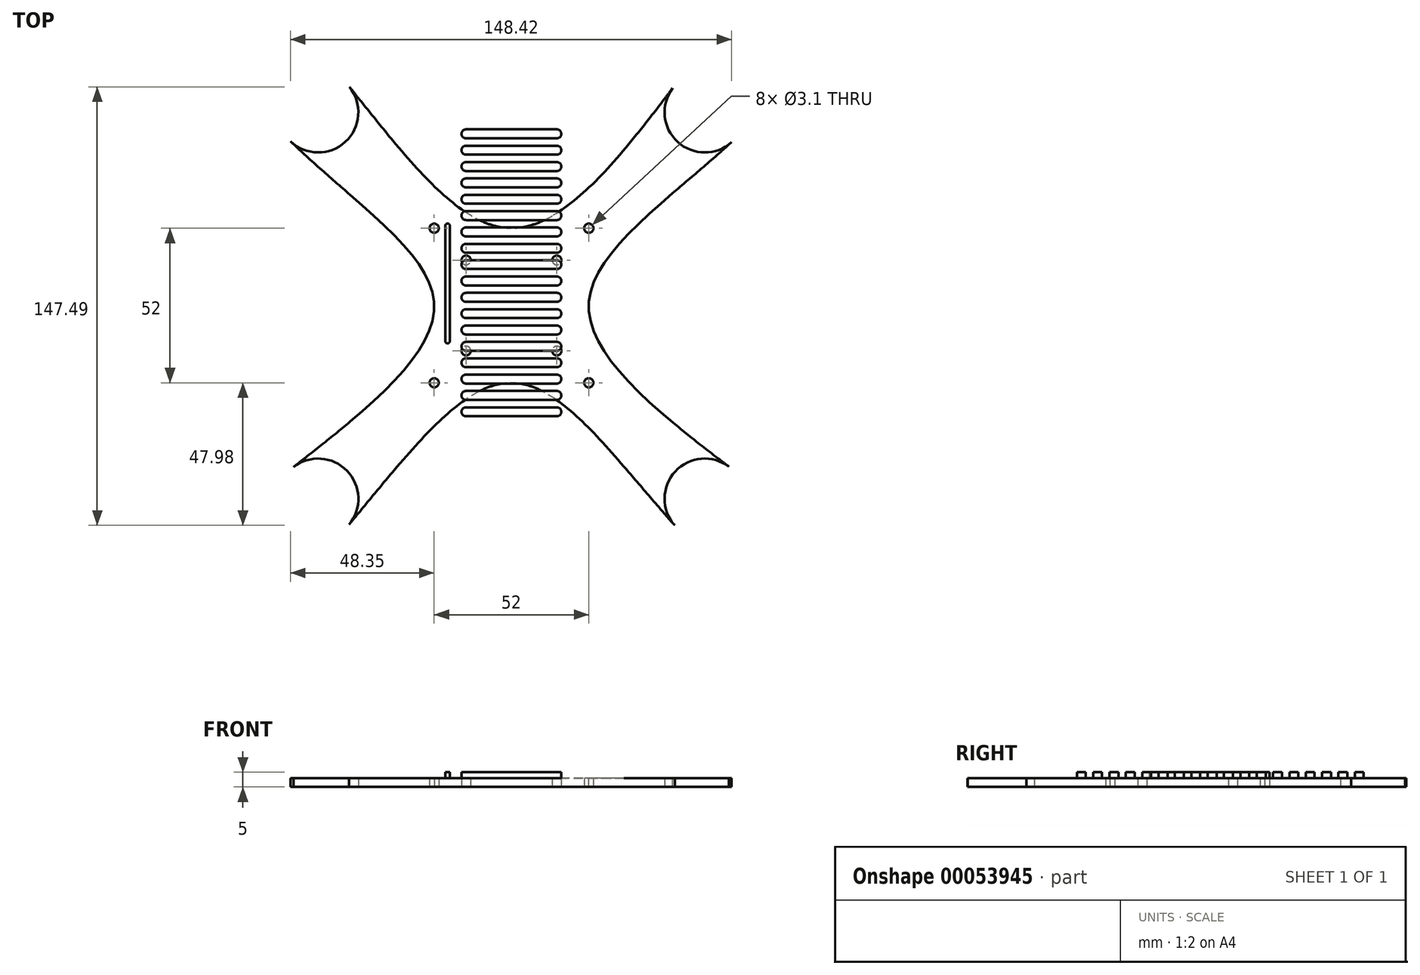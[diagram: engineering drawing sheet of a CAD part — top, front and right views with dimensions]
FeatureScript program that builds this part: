
annotation { "Feature Type Name" : "Feature", "Feature Type Description" : "" }
export const myFeature = defineFeature(function(context is Context, id is Id, definition is map)
    precondition{}
    {
        {
            var Q0;
            Q0=qCreatedBy(makeId("Top.planeOp"),FACE);
            var sketch = newSketch(context, id + "F0", { "sketchPlane" : qUnion([Q0])});
            skLineSegment(sketch, "E0.rect.bottom", {"start": v(-65, -65) * mm, "end": v(65, -65) * mm, "construction": true});
            skLineSegment(sketch, "E0.rect.top", {"start": v(-65, 65) * mm, "end": v(65, 65) * mm, "construction": true});
            skLineSegment(sketch, "E0.rect.left", {"start": v(-65, -65) * mm, "end": v(-65, 65) * mm, "construction": true});
            skLineSegment(sketch, "E0.rect.right", {"start": v(65, -65) * mm, "end": v(65, 65) * mm, "construction": true});
            skPoint(sketch, "E0.rect.middle", {"position": v(0, 0) * mm});
            skCircle(sketch, "E1", {"center": v(-65, 65) * mm, "radius": 50.75 * mm, "construction": true});
            skCircle(sketch, "E2", {"center": v(65, 65) * mm, "radius": 50.75 * mm, "construction": true});
            skCircle(sketch, "E3", {"center": v(65, -65) * mm, "radius": 50.75 * mm, "construction": true});
            skCircle(sketch, "E4", {"center": v(-65, -65) * mm, "radius": 50.75 * mm, "construction": true});
            skArc(sketch, "E5", {"start": v(-77.6, 69.86) * mm, "mid": v(-55.45, 55.45) * mm, "end": v(-69.86, 77.6) * mm});
            skArc(sketch, "E6", {"start": v(69.86, 77.6) * mm, "mid": v(55.45, 55.45) * mm, "end": v(77.6, 69.86) * mm});
            skArc(sketch, "E7", {"start": v(77.6, -69.86) * mm, "mid": v(55.45, -55.45) * mm, "end": v(69.86, -77.6) * mm});
            skArc(sketch, "E8", {"start": v(-69.86, -77.6) * mm, "mid": v(-55.45, -55.45) * mm, "end": v(-77.6, -69.86) * mm});
            skLineSegment(sketch, "E9.rect.bottom", {"start": v(26, -26) * mm, "end": v(-26, -26) * mm, "construction": true});
            skLineSegment(sketch, "E9.rect.top", {"start": v(26, 26) * mm, "end": v(-26, 26) * mm, "construction": true});
            skLineSegment(sketch, "E9.rect.left", {"start": v(26, -26) * mm, "end": v(26, 26) * mm, "construction": true});
            skLineSegment(sketch, "E9.rect.right", {"start": v(-26, -26) * mm, "end": v(-26, 26) * mm, "construction": true});
            skFitSpline(sketch, "E10", {"points": [v(-74.35, 55.26) * mm, v(-26, 0) * mm, v(-73.36, -54.4) * mm], "startDerivative": vector(138.42, -132.82) * mm, "endDerivative": vector(-144.38, -113.88) * mm});
            skFitSpline(sketch, "E11", {"points": [v(74.07, 55) * mm, v(26, 0) * mm, v(73.19, -54.27) * mm], "startDerivative": vector(-139.4, -126.45) * mm, "endDerivative": vector(143.94, -109.76) * mm});
            skFitSpline(sketch, "E12", {"points": [v(54.92, -73.98) * mm, v(0, -26) * mm, v(-54.66, -73.68) * mm], "startDerivative": vector(-126.12, 141.5) * mm, "endDerivative": vector(-120.97, -144.22) * mm});
            skFitSpline(sketch, "E13", {"points": [v(-54.52, 73.5) * mm, v(0, 26) * mm, v(54.26, 73.17) * mm], "startDerivative": vector(114.67, -141.24) * mm, "endDerivative": vector(108.47, 142.58) * mm});
            skLineSegment(sketch, "E14.rect.bottom", {"start": v(-15.25, -15.25) * mm, "end": v(15.25, -15.25) * mm, "construction": true});
            skLineSegment(sketch, "E14.rect.top", {"start": v(-15.25, 15.25) * mm, "end": v(15.25, 15.25) * mm, "construction": true});
            skLineSegment(sketch, "E14.rect.left", {"start": v(-15.25, -15.25) * mm, "end": v(-15.25, 15.25) * mm, "construction": true});
            skLineSegment(sketch, "E14.rect.right", {"start": v(15.25, -15.25) * mm, "end": v(15.25, 15.25) * mm, "construction": true});
            skArc(sketch, "E15", {"start": v(-4.8, 73.17) * mm, "mid": v(-17.28, 102.6) * mm, "end": v(-42.96, 121.6) * mm});
            skArc(sketch, "E16", {"start": v(4.8, 73.17) * mm, "mid": v(17.28, 102.6) * mm, "end": v(42.96, 121.6) * mm});
            skArc(sketch, "E17", {"start": v(73.17, -4.8) * mm, "mid": v(102.6, -17.28) * mm, "end": v(121.6, -42.96) * mm});
            skArc(sketch, "E18", {"start": v(-4.8, -73.17) * mm, "mid": v(-17.28, -102.6) * mm, "end": v(-42.96, -121.6) * mm});
            skArc(sketch, "E19.0", {"start": v(-4.6, 90.96) * mm, "mid": v(-19.8, 112.75) * mm, "end": v(-42.39, 126.74) * mm});
            skArc(sketch, "E20.0", {"start": v(4.6, 90.96) * mm, "mid": v(19.8, 112.75) * mm, "end": v(42.39, 126.74) * mm});
            skLineSegment(sketch, "E21.0.left", {"start": v(-47.27, 67.5) * mm, "end": v(-9.76, 67.5) * mm});
            skLineSegment(sketch, "E22.1.right", {"start": v(-47.17, -67.5) * mm, "end": v(-9.76, -67.5) * mm});
            skLineSegment(sketch, "E23.0.right", {"start": v(67.5, -47.45) * mm, "end": v(67.5, -9.76) * mm});
            skArc(sketch, "E24.trimOffspring", {"start": v(-4.6, -90.96) * mm, "mid": v(-19.8, -112.75) * mm, "end": v(-42.39, -126.74) * mm});
            skArc(sketch, "E25.trimOffspring", {"start": v(90.96, -4.6) * mm, "mid": v(112.75, -19.8) * mm, "end": v(126.74, -42.39) * mm});
            skLineSegment(sketch, "E26.trimOffspring", {"start": v(-35.06, 62.5) * mm, "end": v(35.61, 62.5) * mm});
            skLineSegment(sketch, "E27.trimOffspring", {"start": v(-62.5, -35.22) * mm, "end": v(-62.5, 33.4) * mm});
            skLineSegment(sketch, "E28.trimOffspring", {"start": v(-67.5, -47.35) * mm, "end": v(-67.5, -9.76) * mm});
            skLineSegment(sketch, "E29.trimOffspring", {"start": v(-34.67, -62.5) * mm, "end": v(34.1, -62.5) * mm});
            skLineSegment(sketch, "E30.trimOffspring", {"start": v(62.5, -35.55) * mm, "end": v(62.5, 34) * mm});
            skPoint(sketch, "E31.visualSharp", {"position": v(-74.9, 0) * mm});
            skArc(sketch, "E31.filletArc", {"start": v(-90.96, -4.6) * mm, "mid": v(-87.94, 0) * mm, "end": v(-90.96, 4.6) * mm});
            skPoint(sketch, "E32.visualSharp", {"position": v(0, 74.9) * mm});
            skArc(sketch, "E32.filletArc", {"start": v(-4.6, 90.96) * mm, "mid": v(0, 87.94) * mm, "end": v(4.6, 90.96) * mm});
            skPoint(sketch, "E33.visualSharp", {"position": v(74.9, 0) * mm});
            skArc(sketch, "E33.filletArc", {"start": v(90.96, 4.6) * mm, "mid": v(87.94, 0) * mm, "end": v(90.96, -4.6) * mm});
            skPoint(sketch, "E34.visualSharp", {"position": v(0, -74.9) * mm});
            skArc(sketch, "E34.filletArc", {"start": v(4.6, -90.96) * mm, "mid": v(0, -87.94) * mm, "end": v(-4.6, -90.96) * mm});
            skLineSegment(sketch, "E35.trimOffspring", {"start": v(9.76, 67.5) * mm, "end": v(47.45, 67.5) * mm});
            skLineSegment(sketch, "E36.trimOffspring", {"start": v(67.5, 9.76) * mm, "end": v(67.5, 46.9) * mm});
            skLineSegment(sketch, "E37.trimOffspring", {"start": v(-67.5, 9.76) * mm, "end": v(-67.5, 46.68) * mm});
            skLineSegment(sketch, "E38.trimOffspring", {"start": v(9.76, -67.5) * mm, "end": v(46.96, -67.5) * mm});
            skPoint(sketch, "E39.visualSharp", {"position": v(67.5, 4.3) * mm});
            skArc(sketch, "E39.filletArc", {"start": v(67.5, 9.76) * mm, "mid": v(69.21, 6) * mm, "end": v(73.17, 4.8) * mm});
            skPoint(sketch, "E40.visualSharp", {"position": v(67.5, -4.3) * mm});
            skArc(sketch, "E40.filletArc", {"start": v(73.17, -4.8) * mm, "mid": v(69.21, -6) * mm, "end": v(67.5, -9.76) * mm});
            skPoint(sketch, "E41.visualSharp", {"position": v(4.3, 67.5) * mm});
            skArc(sketch, "E41.filletArc", {"start": v(4.8, 73.17) * mm, "mid": v(6, 69.21) * mm, "end": v(9.76, 67.5) * mm});
            skPoint(sketch, "E42.visualSharp", {"position": v(-4.3, 67.5) * mm});
            skArc(sketch, "E42.filletArc", {"start": v(-9.76, 67.5) * mm, "mid": v(-6, 69.21) * mm, "end": v(-4.8, 73.17) * mm});
            skPoint(sketch, "E43.visualSharp", {"position": v(-67.5, 4.3) * mm});
            skArc(sketch, "E43.filletArc", {"start": v(-73.17, 4.8) * mm, "mid": v(-69.21, 6) * mm, "end": v(-67.5, 9.76) * mm});
            skPoint(sketch, "E44.visualSharp", {"position": v(-67.5, -4.3) * mm});
            skArc(sketch, "E44.filletArc", {"start": v(-67.5, -9.76) * mm, "mid": v(-69.21, -6) * mm, "end": v(-73.17, -4.8) * mm});
            skPoint(sketch, "E45.visualSharp", {"position": v(-4.3, -67.5) * mm});
            skArc(sketch, "E45.filletArc", {"start": v(-4.8, -73.17) * mm, "mid": v(-6, -69.21) * mm, "end": v(-9.76, -67.5) * mm});
            skPoint(sketch, "E46.visualSharp", {"position": v(4.3, -67.5) * mm});
            skArc(sketch, "E46.filletArc", {"start": v(9.76, -67.5) * mm, "mid": v(6, -69.21) * mm, "end": v(4.8, -73.17) * mm});
            skPoint(sketch, "E47.visualSharp", {"position": v(46.05, 62.5) * mm});
            skArc(sketch, "E47.filletArc", {"start": v(39.46, 54.3) * mm, "mid": v(40.14, 59.63) * mm, "end": v(35.61, 62.5) * mm});
            skPoint(sketch, "E48.visualSharp", {"position": v(-45.64, 62.5) * mm});
            skArc(sketch, "E48.filletArc", {"start": v(-35.06, 62.5) * mm, "mid": v(-39.6, 59.61) * mm, "end": v(-38.89, 54.28) * mm});
            skPoint(sketch, "E49.visualSharp", {"position": v(-62.5, 44.43) * mm});
            skArc(sketch, "E49.filletArc", {"start": v(-54.2, 37.17) * mm, "mid": v(-59.57, 37.96) * mm, "end": v(-62.5, 33.4) * mm});
            skPoint(sketch, "E50.visualSharp", {"position": v(-62.5, -45.8) * mm});
            skArc(sketch, "E50.filletArc", {"start": v(-62.5, -35.22) * mm, "mid": v(-59.6, -39.76) * mm, "end": v(-54.28, -39.05) * mm});
            skPoint(sketch, "E51.visualSharp", {"position": v(-45.38, -62.5) * mm});
            skArc(sketch, "E51.filletArc", {"start": v(-38.48, -54.26) * mm, "mid": v(-39.21, -59.6) * mm, "end": v(-34.67, -62.5) * mm});
            skPoint(sketch, "E52.visualSharp", {"position": v(44.96, -62.5) * mm});
            skArc(sketch, "E52.filletArc", {"start": v(34.1, -62.5) * mm, "mid": v(38.64, -59.58) * mm, "end": v(37.88, -54.23) * mm});
            skPoint(sketch, "E53.visualSharp", {"position": v(62.5, -46.02) * mm});
            skArc(sketch, "E53.filletArc", {"start": v(54.3, -39.4) * mm, "mid": v(59.62, -40.08) * mm, "end": v(62.5, -35.55) * mm});
            skPoint(sketch, "E54.visualSharp", {"position": v(62.5, 44.86) * mm});
            skArc(sketch, "E54.filletArc", {"start": v(62.5, 34) * mm, "mid": v(59.58, 38.54) * mm, "end": v(54.24, 37.78) * mm});
            skPoint(sketch, "E55.visualSharp", {"position": v(67.5, 49.17) * mm});
            skArc(sketch, "E55.filletArc", {"start": v(69.2, 50.66) * mm, "mid": v(67.95, 48.96) * mm, "end": v(67.5, 46.9) * mm});
            skPoint(sketch, "E56.visualSharp", {"position": v(49.92, 67.5) * mm});
            skArc(sketch, "E56.filletArc", {"start": v(47.45, 67.5) * mm, "mid": v(49.67, 68.02) * mm, "end": v(51.43, 69.46) * mm});
            skPoint(sketch, "E57.visualSharp", {"position": v(-49.67, 67.5) * mm});
            skArc(sketch, "E57.filletArc", {"start": v(-51.17, 69.36) * mm, "mid": v(-49.43, 67.99) * mm, "end": v(-47.27, 67.5) * mm});
            skPoint(sketch, "E58.visualSharp", {"position": v(-67.5, 48.9) * mm});
            skArc(sketch, "E58.filletArc", {"start": v(-67.5, 46.68) * mm, "mid": v(-67.92, 48.7) * mm, "end": v(-69.12, 50.37) * mm});
            skPoint(sketch, "E59.visualSharp", {"position": v(-67.5, -49.77) * mm});
            skArc(sketch, "E59.filletArc", {"start": v(-69.4, -51.28) * mm, "mid": v(-68, -49.53) * mm, "end": v(-67.5, -47.35) * mm});
            skPoint(sketch, "E60.visualSharp", {"position": v(-49.52, -67.5) * mm});
            skArc(sketch, "E60.filletArc", {"start": v(-47.17, -67.5) * mm, "mid": v(-49.3, -67.97) * mm, "end": v(-51.02, -69.3) * mm});
            skPoint(sketch, "E61.visualSharp", {"position": v(49.25, -67.5) * mm});
            skArc(sketch, "E61.filletArc", {"start": v(50.74, -69.22) * mm, "mid": v(49.04, -67.95) * mm, "end": v(46.96, -67.5) * mm});
            skPoint(sketch, "E62.visualSharp", {"position": v(67.5, -49.9) * mm});
            skArc(sketch, "E62.filletArc", {"start": v(67.5, -47.45) * mm, "mid": v(68.02, -49.66) * mm, "end": v(69.46, -51.41) * mm});
            skLineSegment(sketch, "E63", {"start": v(-65, 65) * mm, "end": v(-111.5, 111.5) * mm, "construction": true});
            skLineSegment(sketch, "E64", {"start": v(65, 65) * mm, "end": v(111.5, 111.5) * mm, "construction": true});
            skLineSegment(sketch, "E65", {"start": v(65, -65) * mm, "end": v(111.5, -111.5) * mm, "construction": true});
            skLineSegment(sketch, "E66", {"start": v(-65, -65) * mm, "end": v(-111.5, -111.5) * mm, "construction": true});
            skLineSegment(sketch, "E67.0.left", {"start": v(-78.73, 75.2) * mm, "end": v(-105.83, 102.3) * mm});
            skLineSegment(sketch, "E67.0.right", {"start": v(-75.2, 78.73) * mm, "end": v(-102.3, 105.83) * mm});
            skLineSegment(sketch, "E67.1.left", {"start": v(75.2, 78.73) * mm, "end": v(102.3, 105.83) * mm});
            skLineSegment(sketch, "E67.1.right", {"start": v(78.73, 75.2) * mm, "end": v(105.83, 102.3) * mm});
            skLineSegment(sketch, "E67.2.left", {"start": v(78.73, -75.2) * mm, "end": v(105.83, -102.3) * mm});
            skLineSegment(sketch, "E67.2.right", {"start": v(75.2, -78.73) * mm, "end": v(102.3, -105.83) * mm});
            skLineSegment(sketch, "E67.3.left", {"start": v(-75.2, -78.73) * mm, "end": v(-102.3, -105.83) * mm});
            skLineSegment(sketch, "E67.3.right", {"start": v(-78.73, -75.2) * mm, "end": v(-105.83, -102.3) * mm});
            skLineSegment(sketch, "E68.trimOffspring", {"start": v(-113.23, 109.7) * mm, "end": v(-113.26, 109.72) * mm});
            skLineSegment(sketch, "E69.trimOffspring", {"start": v(-109.7, 113.23) * mm, "end": v(-109.72, 113.26) * mm});
            skArc(sketch, "E70.trimOffspring", {"start": v(-113.35, 101.79) * mm, "mid": v(-123.85, 80.08) * mm, "end": v(-125.08, 56) * mm});
            skLineSegment(sketch, "E71.trimOffspring", {"start": v(113.23, 109.7) * mm, "end": v(113.26, 109.72) * mm});
            skLineSegment(sketch, "E72.trimOffspring", {"start": v(109.7, 113.23) * mm, "end": v(109.72, 113.26) * mm});
            skArc(sketch, "E73.trimOffspring", {"start": v(113.35, 101.79) * mm, "mid": v(123.85, 80.08) * mm, "end": v(125.08, 56) * mm});
            skLineSegment(sketch, "E74.trimOffspring", {"start": v(113.23, -109.7) * mm, "end": v(113.26, -109.72) * mm});
            skLineSegment(sketch, "E75.trimOffspring", {"start": v(109.7, -113.23) * mm, "end": v(109.72, -113.26) * mm});
            skArc(sketch, "E76.trimOffspring", {"start": v(101.79, -113.35) * mm, "mid": v(80.08, -123.85) * mm, "end": v(56, -125.08) * mm});
            skArc(sketch, "E77.trimOffspring", {"start": v(-113.35, -101.79) * mm, "mid": v(-123.85, -80.08) * mm, "end": v(-125.08, -56) * mm});
            skLineSegment(sketch, "E78.trimOffspring", {"start": v(-113.23, -109.7) * mm, "end": v(-113.26, -109.72) * mm});
            skLineSegment(sketch, "E79.trimOffspring", {"start": v(-109.7, -113.23) * mm, "end": v(-109.72, -113.26) * mm});
            skPoint(sketch, "E80.visualSharp", {"position": v(106.15, 109.69) * mm});
            skArc(sketch, "E80.filletArc", {"start": v(102.3, 105.83) * mm, "mid": v(103.75, 109.7) * mm, "end": v(101.79, 113.35) * mm});
            skPoint(sketch, "E81.visualSharp", {"position": v(109.69, 106.15) * mm});
            skArc(sketch, "E81.filletArc", {"start": v(113.35, 101.79) * mm, "mid": v(109.7, 103.75) * mm, "end": v(105.83, 102.3) * mm});
            skPoint(sketch, "E82.visualSharp", {"position": v(76.15, 72.61) * mm});
            skArc(sketch, "E82.filletArc", {"start": v(78.73, 75.2) * mm, "mid": v(77.37, 72.7) * mm, "end": v(77.6, 69.86) * mm});
            skPoint(sketch, "E83.visualSharp", {"position": v(72.61, 76.15) * mm});
            skArc(sketch, "E83.filletArc", {"start": v(69.86, 77.6) * mm, "mid": v(72.7, 77.37) * mm, "end": v(75.2, 78.73) * mm});
            skPoint(sketch, "E84.visualSharp", {"position": v(-72.61, 76.15) * mm});
            skArc(sketch, "E84.filletArc", {"start": v(-75.2, 78.73) * mm, "mid": v(-72.7, 77.37) * mm, "end": v(-69.86, 77.6) * mm});
            skPoint(sketch, "E85.visualSharp", {"position": v(-76.15, 72.61) * mm});
            skArc(sketch, "E85.filletArc", {"start": v(-77.6, 69.86) * mm, "mid": v(-77.37, 72.7) * mm, "end": v(-78.73, 75.2) * mm});
            skPoint(sketch, "E86.visualSharp", {"position": v(-106.15, 109.69) * mm});
            skArc(sketch, "E86.filletArc", {"start": v(-101.79, 113.35) * mm, "mid": v(-103.75, 109.7) * mm, "end": v(-102.3, 105.83) * mm});
            skPoint(sketch, "E87.visualSharp", {"position": v(-109.69, 106.15) * mm});
            skArc(sketch, "E87.filletArc", {"start": v(-105.83, 102.3) * mm, "mid": v(-109.7, 103.75) * mm, "end": v(-113.35, 101.79) * mm});
            skPoint(sketch, "E88.visualSharp", {"position": v(76.15, -72.61) * mm});
            skArc(sketch, "E88.filletArc", {"start": v(77.6, -69.86) * mm, "mid": v(77.37, -72.7) * mm, "end": v(78.73, -75.2) * mm});
            skPoint(sketch, "E89.visualSharp", {"position": v(109.69, -106.15) * mm});
            skArc(sketch, "E89.filletArc", {"start": v(105.83, -102.3) * mm, "mid": v(109.7, -103.75) * mm, "end": v(113.35, -101.79) * mm});
            skPoint(sketch, "E90.visualSharp", {"position": v(106.15, -109.69) * mm});
            skArc(sketch, "E90.filletArc", {"start": v(101.79, -113.35) * mm, "mid": v(103.75, -109.7) * mm, "end": v(102.3, -105.83) * mm});
            skPoint(sketch, "E91.visualSharp", {"position": v(72.61, -76.15) * mm});
            skArc(sketch, "E91.filletArc", {"start": v(75.2, -78.73) * mm, "mid": v(72.7, -77.37) * mm, "end": v(69.86, -77.6) * mm});
            skPoint(sketch, "E92.visualSharp", {"position": v(-72.61, -76.15) * mm});
            skArc(sketch, "E92.filletArc", {"start": v(-69.86, -77.6) * mm, "mid": v(-72.7, -77.37) * mm, "end": v(-75.2, -78.73) * mm});
            skPoint(sketch, "E93.visualSharp", {"position": v(-76.15, -72.61) * mm});
            skArc(sketch, "E93.filletArc", {"start": v(-78.73, -75.2) * mm, "mid": v(-77.37, -72.7) * mm, "end": v(-77.6, -69.86) * mm});
            skPoint(sketch, "E94.visualSharp", {"position": v(-106.15, -109.69) * mm});
            skArc(sketch, "E94.filletArc", {"start": v(-102.3, -105.83) * mm, "mid": v(-103.75, -109.7) * mm, "end": v(-101.79, -113.35) * mm});
            skPoint(sketch, "E95.visualSharp", {"position": v(-109.69, -106.15) * mm});
            skArc(sketch, "E95.filletArc", {"start": v(-113.35, -101.79) * mm, "mid": v(-109.7, -103.75) * mm, "end": v(-105.83, -102.3) * mm});
            skCircle(sketch, "E96", {"center": v(-15.25, 15.25) * mm, "radius": 1.55 * mm});
            skCircle(sketch, "E97", {"center": v(15.25, 15.25) * mm, "radius": 1.55 * mm});
            skCircle(sketch, "E98", {"center": v(15.25, -15.25) * mm, "radius": 1.55 * mm});
            skCircle(sketch, "E99", {"center": v(-15.25, -15.25) * mm, "radius": 1.55 * mm});
            skCircle(sketch, "E100", {"center": v(-65, 65) * mm, "radius": 4.5 * mm});
            skCircle(sketch, "E101", {"center": v(65, 65) * mm, "radius": 4.5 * mm});
            skCircle(sketch, "E102", {"center": v(65, -65) * mm, "radius": 4.5 * mm});
            skCircle(sketch, "E103", {"center": v(-65, -65) * mm, "radius": 4.5 * mm});
            skCircle(sketch, "E104", {"center": v(-26, 26) * mm, "radius": 1.55 * mm});
            skCircle(sketch, "E105", {"center": v(26, 26) * mm, "radius": 1.55 * mm});
            skCircle(sketch, "E106", {"center": v(-26, -26) * mm, "radius": 1.55 * mm});
            skCircle(sketch, "E107", {"center": v(26, -26) * mm, "radius": 1.55 * mm});
            skLineSegment(sketch, "E108", {"start": v(65, 57) * mm, "end": v(65, 55.5) * mm});
            skLineSegment(sketch, "E109", {"start": v(57, 65) * mm, "end": v(55.5, 65) * mm});
            skLineSegment(sketch, "E110", {"start": v(73, 65) * mm, "end": v(74.5, 65) * mm});
            skLineSegment(sketch, "E111", {"start": v(65, 73) * mm, "end": v(65, 74.5) * mm});
            skArc(sketch, "E112.0.startCap", {"start": v(73, 63.5) * mm, "mid": v(71.5, 65) * mm, "end": v(73, 66.5) * mm});
            skArc(sketch, "E112.0.endCap", {"start": v(74.5, 66.5) * mm, "mid": v(76, 65) * mm, "end": v(74.5, 63.5) * mm});
            skLineSegment(sketch, "E112.0.left", {"start": v(73, 66.5) * mm, "end": v(74.5, 66.5) * mm});
            skLineSegment(sketch, "E112.0.right", {"start": v(73, 63.5) * mm, "end": v(74.5, 63.5) * mm});
            skArc(sketch, "E113.0.startCap", {"start": v(66.5, 73) * mm, "mid": v(65, 71.5) * mm, "end": v(63.5, 73) * mm});
            skArc(sketch, "E113.0.endCap", {"start": v(63.5, 74.5) * mm, "mid": v(65, 76) * mm, "end": v(66.5, 74.5) * mm});
            skLineSegment(sketch, "E113.0.left", {"start": v(63.5, 73) * mm, "end": v(63.5, 74.5) * mm});
            skLineSegment(sketch, "E113.0.right", {"start": v(66.5, 73) * mm, "end": v(66.5, 74.5) * mm});
            skArc(sketch, "E114.0.startCap", {"start": v(57, 66.5) * mm, "mid": v(58.5, 65) * mm, "end": v(57, 63.5) * mm});
            skArc(sketch, "E114.0.endCap", {"start": v(55.5, 63.5) * mm, "mid": v(54, 65) * mm, "end": v(55.5, 66.5) * mm});
            skLineSegment(sketch, "E114.0.left", {"start": v(57, 63.5) * mm, "end": v(55.5, 63.5) * mm});
            skLineSegment(sketch, "E114.0.right", {"start": v(57, 66.5) * mm, "end": v(55.5, 66.5) * mm});
            skArc(sketch, "E115.0.startCap", {"start": v(63.5, 57) * mm, "mid": v(65, 58.5) * mm, "end": v(66.5, 57) * mm});
            skArc(sketch, "E115.0.endCap", {"start": v(66.5, 55.5) * mm, "mid": v(65, 54) * mm, "end": v(63.5, 55.5) * mm});
            skLineSegment(sketch, "E115.0.left", {"start": v(66.5, 57) * mm, "end": v(66.5, 55.5) * mm});
            skLineSegment(sketch, "E115.0.right", {"start": v(63.5, 57) * mm, "end": v(63.5, 55.5) * mm});
            skLineSegment(sketch, "E116", {"start": v(0, 153.86) * mm, "end": v(0, -113.26) * mm, "construction": true});
            skArc(sketch, "E117.MirrorCS", {"start": v(-66.5, 55.5) * mm, "mid": v(-65, 54) * mm, "end": v(-63.5, 55.5) * mm});
            skLineSegment(sketch, "E118.MirrorCS", {"start": v(-66.5, 57) * mm, "end": v(-66.5, 55.5) * mm});
            skLineSegment(sketch, "E119.MirrorCS", {"start": v(-63.5, 57) * mm, "end": v(-63.5, 55.5) * mm});
            skArc(sketch, "E120.MirrorCS", {"start": v(-63.5, 57) * mm, "mid": v(-65, 58.5) * mm, "end": v(-66.5, 57) * mm});
            skLineSegment(sketch, "E121.MirrorCS", {"start": v(-65, 57) * mm, "end": v(-65, 55.5) * mm});
            skArc(sketch, "E122.MirrorCS", {"start": v(-73, 63.5) * mm, "mid": v(-71.5, 65) * mm, "end": v(-73, 66.5) * mm});
            skLineSegment(sketch, "E123.MirrorCS", {"start": v(-73, 63.5) * mm, "end": v(-74.5, 63.5) * mm});
            skLineSegment(sketch, "E124.MirrorCS", {"start": v(-73, 66.5) * mm, "end": v(-74.5, 66.5) * mm});
            skLineSegment(sketch, "E125.MirrorCS", {"start": v(-73, 65) * mm, "end": v(-74.5, 65) * mm});
            skArc(sketch, "E126.MirrorCS", {"start": v(-74.5, 66.5) * mm, "mid": v(-76, 65) * mm, "end": v(-74.5, 63.5) * mm});
            skLineSegment(sketch, "E127.MirrorCS", {"start": v(-57, 63.5) * mm, "end": v(-55.5, 63.5) * mm});
            skArc(sketch, "E128.MirrorCS", {"start": v(-55.5, 63.5) * mm, "mid": v(-54, 65) * mm, "end": v(-55.5, 66.5) * mm});
            skLineSegment(sketch, "E129.MirrorCS", {"start": v(-66.5, 73) * mm, "end": v(-66.5, 74.5) * mm});
            skLineSegment(sketch, "E130.MirrorCS", {"start": v(-57, 66.5) * mm, "end": v(-55.5, 66.5) * mm});
            skArc(sketch, "E131.MirrorCS", {"start": v(-57, 66.5) * mm, "mid": v(-58.5, 65) * mm, "end": v(-57, 63.5) * mm});
            skArc(sketch, "E132.MirrorCS", {"start": v(-63.5, 74.5) * mm, "mid": v(-65, 76) * mm, "end": v(-66.5, 74.5) * mm});
            skArc(sketch, "E133.MirrorCS", {"start": v(-66.5, 73) * mm, "mid": v(-65, 71.5) * mm, "end": v(-63.5, 73) * mm});
            skLineSegment(sketch, "E134", {"start": v(-63.5, 74.5) * mm, "end": v(-63.5, 73) * mm});
            skLineSegment(sketch, "E135", {"start": v(125.68, 0) * mm, "end": v(-117.28, 0) * mm, "construction": true});
            skArc(sketch, "E136.MirrorCS", {"start": v(-66.5, -55.5) * mm, "mid": v(-65, -54) * mm, "end": v(-63.5, -55.5) * mm});
            skLineSegment(sketch, "E137.MirrorCS", {"start": v(-63.5, -57) * mm, "end": v(-63.5, -55.5) * mm});
            skLineSegment(sketch, "E138.MirrorCS", {"start": v(-66.5, -57) * mm, "end": v(-66.5, -55.5) * mm});
            skLineSegment(sketch, "E139.MirrorCS", {"start": v(-65, -57) * mm, "end": v(-65, -55.5) * mm});
            skArc(sketch, "E140.MirrorCS", {"start": v(-63.5, -57) * mm, "mid": v(-65, -58.5) * mm, "end": v(-66.5, -57) * mm});
            skArc(sketch, "E141.MirrorCS", {"start": v(-74.5, -66.5) * mm, "mid": v(-76, -65) * mm, "end": v(-74.5, -63.5) * mm});
            skLineSegment(sketch, "E142.MirrorCS", {"start": v(-73, -65) * mm, "end": v(-74.5, -65) * mm});
            skLineSegment(sketch, "E143.MirrorCS", {"start": v(-73, -66.5) * mm, "end": v(-74.5, -66.5) * mm});
            skLineSegment(sketch, "E144.MirrorCS", {"start": v(-73, -63.5) * mm, "end": v(-74.5, -63.5) * mm});
            skArc(sketch, "E145.MirrorCS", {"start": v(-73, -63.5) * mm, "mid": v(-71.5, -65) * mm, "end": v(-73, -66.5) * mm});
            skLineSegment(sketch, "E146.MirrorCS", {"start": v(-57, -63.5) * mm, "end": v(-55.5, -63.5) * mm});
            skLineSegment(sketch, "E147.MirrorCS", {"start": v(-57, -66.5) * mm, "end": v(-55.5, -66.5) * mm});
            skArc(sketch, "E148.MirrorCS", {"start": v(-57, -66.5) * mm, "mid": v(-58.5, -65) * mm, "end": v(-57, -63.5) * mm});
            skArc(sketch, "E149.MirrorCS", {"start": v(-55.5, -63.5) * mm, "mid": v(-54, -65) * mm, "end": v(-55.5, -66.5) * mm});
            skArc(sketch, "E150.MirrorCS", {"start": v(-66.5, -73) * mm, "mid": v(-65, -71.5) * mm, "end": v(-63.5, -73) * mm});
            skArc(sketch, "E151.MirrorCS", {"start": v(-63.5, -74.5) * mm, "mid": v(-65, -76) * mm, "end": v(-66.5, -74.5) * mm});
            skLineSegment(sketch, "E152.MirrorCS", {"start": v(-66.5, -73) * mm, "end": v(-66.5, -74.5) * mm});
            skLineSegment(sketch, "E153.MirrorCS", {"start": v(-63.5, -74.5) * mm, "end": v(-63.5, -73) * mm});
            skLineSegment(sketch, "E154.MirrorCS", {"start": v(65, -57) * mm, "end": v(65, -55.5) * mm});
            skLineSegment(sketch, "E155.MirrorCS", {"start": v(63.5, -57) * mm, "end": v(63.5, -55.5) * mm});
            skLineSegment(sketch, "E156.MirrorCS", {"start": v(66.5, -57) * mm, "end": v(66.5, -55.5) * mm});
            skArc(sketch, "E157.MirrorCS", {"start": v(66.5, -55.5) * mm, "mid": v(65, -54) * mm, "end": v(63.5, -55.5) * mm});
            skArc(sketch, "E158.MirrorCS", {"start": v(63.5, -57) * mm, "mid": v(65, -58.5) * mm, "end": v(66.5, -57) * mm});
            skArc(sketch, "E159.MirrorCS", {"start": v(74.5, -66.5) * mm, "mid": v(76, -65) * mm, "end": v(74.5, -63.5) * mm});
            skLineSegment(sketch, "E160.MirrorCS", {"start": v(73, -65) * mm, "end": v(74.5, -65) * mm});
            skLineSegment(sketch, "E161.MirrorCS", {"start": v(73, -63.5) * mm, "end": v(74.5, -63.5) * mm});
            skArc(sketch, "E162.MirrorCS", {"start": v(73, -63.5) * mm, "mid": v(71.5, -65) * mm, "end": v(73, -66.5) * mm});
            skLineSegment(sketch, "E163.MirrorCS", {"start": v(73, -66.5) * mm, "end": v(74.5, -66.5) * mm});
            skLineSegment(sketch, "E164.MirrorCS", {"start": v(57, -66.5) * mm, "end": v(55.5, -66.5) * mm});
            skLineSegment(sketch, "E165.MirrorCS", {"start": v(57, -63.5) * mm, "end": v(55.5, -63.5) * mm});
            skArc(sketch, "E166.MirrorCS", {"start": v(55.5, -63.5) * mm, "mid": v(54, -65) * mm, "end": v(55.5, -66.5) * mm});
            skLineSegment(sketch, "E167.MirrorCS", {"start": v(57, -65) * mm, "end": v(55.5, -65) * mm});
            skArc(sketch, "E168.MirrorCS", {"start": v(57, -66.5) * mm, "mid": v(58.5, -65) * mm, "end": v(57, -63.5) * mm});
            skArc(sketch, "E169.MirrorCS", {"start": v(63.5, -74.5) * mm, "mid": v(65, -76) * mm, "end": v(66.5, -74.5) * mm});
            skLineSegment(sketch, "E170.MirrorCS", {"start": v(65, -73) * mm, "end": v(65, -74.5) * mm});
            skLineSegment(sketch, "E171.MirrorCS", {"start": v(63.5, -73) * mm, "end": v(63.5, -74.5) * mm});
            skLineSegment(sketch, "E172.MirrorCS", {"start": v(66.5, -73) * mm, "end": v(66.5, -74.5) * mm});
            skArc(sketch, "E173.MirrorCS", {"start": v(66.5, -73) * mm, "mid": v(65, -71.5) * mm, "end": v(63.5, -73) * mm});
            skArc(sketch, "E174", {"start": v(-122.17, 48.12) * mm, "mid": v(-122.26, 49.77) * mm, "end": v(-123, 51.24) * mm});
            skArc(sketch, "E175.MirrorC", {"start": v(-46.45, 122.85) * mm, "mid": v(-49.77, 122.26) * mm, "end": v(-52.36, 124.42) * mm});
            skArc(sketch, "E176.MirrorC", {"start": v(-130, 49.75) * mm, "mid": v(-129.99, 47.71) * mm, "end": v(-128.98, 45.94) * mm});
            skArc(sketch, "E177.MirrorC", {"start": v(-48.12, 122.17) * mm, "mid": v(-49.77, 122.26) * mm, "end": v(-51.24, 123) * mm});
            skArc(sketch, "E178.MirrorC", {"start": v(130, 49.75) * mm, "mid": v(129.99, 47.71) * mm, "end": v(128.98, 45.94) * mm});
            skArc(sketch, "E179.MirrorC", {"start": v(48.12, 122.17) * mm, "mid": v(49.77, 122.26) * mm, "end": v(51.24, 123) * mm});
            skArc(sketch, "E180.MirrorC", {"start": v(122.17, -48.12) * mm, "mid": v(122.26, -49.77) * mm, "end": v(123, -51.24) * mm});
            skArc(sketch, "E181.MirrorC", {"start": v(49.75, -130) * mm, "mid": v(47.71, -129.99) * mm, "end": v(45.94, -128.98) * mm});
            skArc(sketch, "E182.MirrorC", {"start": v(-48.12, -122.17) * mm, "mid": v(-49.77, -122.26) * mm, "end": v(-51.24, -123) * mm});
            skArc(sketch, "E183.MirrorC", {"start": v(-122.17, -48.12) * mm, "mid": v(-122.26, -49.77) * mm, "end": v(-123, -51.24) * mm});
            skArc(sketch, "E184.trimOffspring", {"start": v(-126.74, 42.39) * mm, "mid": v(-112.75, 19.8) * mm, "end": v(-90.96, 4.6) * mm});
            skArc(sketch, "E185.trimOffspring", {"start": v(-121.6, 42.96) * mm, "mid": v(-102.6, 17.28) * mm, "end": v(-73.17, 4.8) * mm});
            skArc(sketch, "E186.trimOffspring", {"start": v(-122.85, 46.45) * mm, "mid": v(-122.26, 49.77) * mm, "end": v(-124.42, 52.36) * mm});
            skArc(sketch, "E187.trimOffspring", {"start": v(-129.28, 51.2) * mm, "mid": v(-129.99, 47.71) * mm, "end": v(-127.65, 45.04) * mm});
            skArc(sketch, "E188.trimOffspring", {"start": v(-53.95, 129.81) * mm, "mid": v(-111.5, 111.5) * mm, "end": v(-129.81, 53.95) * mm});
            skArc(sketch, "E189.trimOffspring", {"start": v(-56, 125.08) * mm, "mid": v(-80.08, 123.85) * mm, "end": v(-101.79, 113.35) * mm});
            skArc(sketch, "E190.trimOffspring", {"start": v(-51.2, 129.28) * mm, "mid": v(-47.71, 129.99) * mm, "end": v(-45.04, 127.65) * mm});
            skArc(sketch, "E191.trimOffspring", {"start": v(-49.75, 130) * mm, "mid": v(-47.71, 129.99) * mm, "end": v(-45.94, 128.98) * mm});
            skArc(sketch, "E192.trimOffspring", {"start": v(49.75, 130) * mm, "mid": v(47.71, 129.99) * mm, "end": v(45.94, 128.98) * mm});
            skArc(sketch, "E193.trimOffspring", {"start": v(53.95, 129.81) * mm, "mid": v(111.5, 111.5) * mm, "end": v(129.81, 53.95) * mm});
            skArc(sketch, "E194.trimOffspring", {"start": v(56, 125.08) * mm, "mid": v(80.08, 123.85) * mm, "end": v(101.79, 113.35) * mm});
            skArc(sketch, "E195.trimOffspring", {"start": v(121.6, 42.96) * mm, "mid": v(102.6, 17.28) * mm, "end": v(73.17, 4.8) * mm});
            skArc(sketch, "E196.trimOffspring", {"start": v(126.74, 42.39) * mm, "mid": v(112.75, 19.8) * mm, "end": v(90.96, 4.6) * mm});
            skArc(sketch, "E197.trimOffspring", {"start": v(122.17, 48.12) * mm, "mid": v(122.26, 49.77) * mm, "end": v(123, 51.24) * mm});
            skArc(sketch, "E198.trimOffspring", {"start": v(-130, -49.75) * mm, "mid": v(-129.99, -47.71) * mm, "end": v(-128.98, -45.94) * mm});
            skArc(sketch, "E199.trimOffspring", {"start": v(-126.74, -42.39) * mm, "mid": v(-112.75, -19.8) * mm, "end": v(-90.96, -4.6) * mm});
            skArc(sketch, "E200.trimOffspring", {"start": v(-121.6, -42.96) * mm, "mid": v(-102.6, -17.28) * mm, "end": v(-73.17, -4.8) * mm});
            skArc(sketch, "E201.trimOffspring", {"start": v(-56, -125.08) * mm, "mid": v(-80.08, -123.85) * mm, "end": v(-101.79, -113.35) * mm});
            skArc(sketch, "E202.trimOffspring", {"start": v(-53.95, -129.81) * mm, "mid": v(-111.5, -111.5) * mm, "end": v(-129.81, -53.95) * mm});
            skArc(sketch, "E203.trimOffspring", {"start": v(-49.75, -130) * mm, "mid": v(-47.71, -129.99) * mm, "end": v(-45.94, -128.98) * mm});
            skArc(sketch, "E204.trimOffspring", {"start": v(42.39, -126.74) * mm, "mid": v(19.8, -112.75) * mm, "end": v(4.6, -90.96) * mm});
            skArc(sketch, "E205.trimOffspring", {"start": v(42.96, -121.6) * mm, "mid": v(17.28, -102.6) * mm, "end": v(4.8, -73.17) * mm});
            skArc(sketch, "E206.trimOffspring", {"start": v(48.12, -122.17) * mm, "mid": v(49.77, -122.26) * mm, "end": v(51.24, -123) * mm});
            skArc(sketch, "E207.trimOffspring", {"start": v(130, -49.75) * mm, "mid": v(129.99, -47.71) * mm, "end": v(128.98, -45.94) * mm});
            skArc(sketch, "E208.trimOffspring", {"start": v(129.81, -53.95) * mm, "mid": v(111.5, -111.5) * mm, "end": v(53.95, -129.81) * mm});
            skPoint(sketch, "E209.visualSharp", {"position": v(-45.04, 127.65) * mm});
            skArc(sketch, "E209.filletArc", {"start": v(-45.94, 128.98) * mm, "mid": v(-44.28, 127.67) * mm, "end": v(-42.39, 126.74) * mm});
            skPoint(sketch, "E210.visualSharp", {"position": v(-46.45, 122.85) * mm});
            skArc(sketch, "E210.filletArc", {"start": v(-42.96, 121.6) * mm, "mid": v(-45.5, 122.23) * mm, "end": v(-48.12, 122.17) * mm});
            skPoint(sketch, "E211.visualSharp", {"position": v(-51.2, 129.28) * mm});
            skArc(sketch, "E211.filletArc", {"start": v(-53.95, 129.81) * mm, "mid": v(-51.84, 129.68) * mm, "end": v(-49.75, 130) * mm});
            skPoint(sketch, "E212.visualSharp", {"position": v(-52.36, 124.42) * mm});
            skArc(sketch, "E212.filletArc", {"start": v(-51.24, 123) * mm, "mid": v(-53.48, 124.36) * mm, "end": v(-56, 125.08) * mm});
            skPoint(sketch, "E213.visualSharp", {"position": v(-124.42, 52.36) * mm});
            skArc(sketch, "E213.filletArc", {"start": v(-125.08, 56) * mm, "mid": v(-124.36, 53.48) * mm, "end": v(-123, 51.24) * mm});
            skPoint(sketch, "E214.visualSharp", {"position": v(-122.85, 46.45) * mm});
            skArc(sketch, "E214.filletArc", {"start": v(-122.17, 48.12) * mm, "mid": v(-122.23, 45.5) * mm, "end": v(-121.6, 42.96) * mm});
            skPoint(sketch, "E215.visualSharp", {"position": v(-129.28, 51.2) * mm});
            skArc(sketch, "E215.filletArc", {"start": v(-130, 49.75) * mm, "mid": v(-129.68, 51.84) * mm, "end": v(-129.81, 53.95) * mm});
            skPoint(sketch, "E216.visualSharp", {"position": v(-127.65, 45.04) * mm});
            skArc(sketch, "E216.filletArc", {"start": v(-126.74, 42.39) * mm, "mid": v(-127.67, 44.28) * mm, "end": v(-128.98, 45.94) * mm});
            skPoint(sketch, "E217.visualSharp", {"position": v(45.04, 127.65) * mm});
            skArc(sketch, "E217.filletArc", {"start": v(42.39, 126.74) * mm, "mid": v(44.28, 127.67) * mm, "end": v(45.94, 128.98) * mm});
            skPoint(sketch, "E218.visualSharp", {"position": v(51.2, 129.28) * mm});
            skArc(sketch, "E218.filletArc", {"start": v(49.75, 130) * mm, "mid": v(51.84, 129.68) * mm, "end": v(53.95, 129.81) * mm});
            skPoint(sketch, "E219.visualSharp", {"position": v(52.36, 124.42) * mm});
            skArc(sketch, "E219.filletArc", {"start": v(56, 125.08) * mm, "mid": v(53.48, 124.36) * mm, "end": v(51.24, 123) * mm});
            skPoint(sketch, "E220.visualSharp", {"position": v(46.45, 122.85) * mm});
            skArc(sketch, "E220.filletArc", {"start": v(48.12, 122.17) * mm, "mid": v(45.5, 122.23) * mm, "end": v(42.96, 121.6) * mm});
            skPoint(sketch, "E221.visualSharp", {"position": v(124.42, 52.36) * mm});
            skArc(sketch, "E221.filletArc", {"start": v(123, 51.24) * mm, "mid": v(124.36, 53.48) * mm, "end": v(125.08, 56) * mm});
            skPoint(sketch, "E222.visualSharp", {"position": v(122.85, 46.45) * mm});
            skArc(sketch, "E222.filletArc", {"start": v(121.6, 42.96) * mm, "mid": v(122.23, 45.5) * mm, "end": v(122.17, 48.12) * mm});
            skPoint(sketch, "E223.visualSharp", {"position": v(127.65, 45.04) * mm});
            skArc(sketch, "E223.filletArc", {"start": v(128.98, 45.94) * mm, "mid": v(127.67, 44.28) * mm, "end": v(126.74, 42.39) * mm});
            skPoint(sketch, "E224.visualSharp", {"position": v(129.28, 51.2) * mm});
            skArc(sketch, "E224.filletArc", {"start": v(129.81, 53.95) * mm, "mid": v(129.68, 51.84) * mm, "end": v(130, 49.75) * mm});
            skArc(sketch, "E225.trimOffspring", {"start": v(125.08, -56) * mm, "mid": v(123.85, -80.08) * mm, "end": v(113.35, -101.79) * mm});
            skPoint(sketch, "E226.visualSharp", {"position": v(127.65, -45.04) * mm});
            skArc(sketch, "E226.filletArc", {"start": v(126.74, -42.39) * mm, "mid": v(127.67, -44.28) * mm, "end": v(128.98, -45.94) * mm});
            skPoint(sketch, "E227.visualSharp", {"position": v(129.28, -51.2) * mm});
            skArc(sketch, "E227.filletArc", {"start": v(130, -49.75) * mm, "mid": v(129.68, -51.84) * mm, "end": v(129.81, -53.95) * mm});
            skPoint(sketch, "E228.visualSharp", {"position": v(124.42, -52.36) * mm});
            skArc(sketch, "E228.filletArc", {"start": v(125.08, -56) * mm, "mid": v(124.36, -53.48) * mm, "end": v(123, -51.24) * mm});
            skPoint(sketch, "E229.visualSharp", {"position": v(122.85, -46.45) * mm});
            skArc(sketch, "E229.filletArc", {"start": v(122.17, -48.12) * mm, "mid": v(122.23, -45.5) * mm, "end": v(121.6, -42.96) * mm});
            skPoint(sketch, "E230.visualSharp", {"position": v(52.36, -124.42) * mm});
            skArc(sketch, "E230.filletArc", {"start": v(51.24, -123) * mm, "mid": v(53.48, -124.36) * mm, "end": v(56, -125.08) * mm});
            skPoint(sketch, "E231.visualSharp", {"position": v(51.2, -129.28) * mm});
            skArc(sketch, "E231.filletArc", {"start": v(53.95, -129.81) * mm, "mid": v(51.84, -129.68) * mm, "end": v(49.75, -130) * mm});
            skPoint(sketch, "E232.visualSharp", {"position": v(45.04, -127.65) * mm});
            skArc(sketch, "E232.filletArc", {"start": v(45.94, -128.98) * mm, "mid": v(44.28, -127.67) * mm, "end": v(42.39, -126.74) * mm});
            skPoint(sketch, "E233.visualSharp", {"position": v(46.45, -122.85) * mm});
            skArc(sketch, "E233.filletArc", {"start": v(42.96, -121.6) * mm, "mid": v(45.5, -122.23) * mm, "end": v(48.12, -122.17) * mm});
            skPoint(sketch, "E234.visualSharp", {"position": v(-46.45, -122.85) * mm});
            skArc(sketch, "E234.filletArc", {"start": v(-48.12, -122.17) * mm, "mid": v(-45.5, -122.23) * mm, "end": v(-42.96, -121.6) * mm});
            skPoint(sketch, "E235.visualSharp", {"position": v(-45.04, -127.65) * mm});
            skArc(sketch, "E235.filletArc", {"start": v(-42.39, -126.74) * mm, "mid": v(-44.28, -127.67) * mm, "end": v(-45.94, -128.98) * mm});
            skPoint(sketch, "E236.visualSharp", {"position": v(-51.2, -129.28) * mm});
            skArc(sketch, "E236.filletArc", {"start": v(-49.75, -130) * mm, "mid": v(-51.84, -129.68) * mm, "end": v(-53.95, -129.81) * mm});
            skPoint(sketch, "E237.visualSharp", {"position": v(-52.36, -124.42) * mm});
            skArc(sketch, "E237.filletArc", {"start": v(-56, -125.08) * mm, "mid": v(-53.48, -124.36) * mm, "end": v(-51.24, -123) * mm});
            skPoint(sketch, "E238.visualSharp", {"position": v(-124.42, -52.36) * mm});
            skArc(sketch, "E238.filletArc", {"start": v(-123, -51.24) * mm, "mid": v(-124.36, -53.48) * mm, "end": v(-125.08, -56) * mm});
            skPoint(sketch, "E239.visualSharp", {"position": v(-122.85, -46.45) * mm});
            skArc(sketch, "E239.filletArc", {"start": v(-121.6, -42.96) * mm, "mid": v(-122.23, -45.5) * mm, "end": v(-122.17, -48.12) * mm});
            skPoint(sketch, "E240.visualSharp", {"position": v(-129.28, -51.2) * mm});
            skArc(sketch, "E240.filletArc", {"start": v(-129.81, -53.95) * mm, "mid": v(-129.68, -51.84) * mm, "end": v(-130, -49.75) * mm});
            skPoint(sketch, "E241.visualSharp", {"position": v(-127.65, -45.04) * mm});
            skArc(sketch, "E241.filletArc", {"start": v(-128.98, -45.94) * mm, "mid": v(-127.67, -44.28) * mm, "end": v(-126.74, -42.39) * mm});
            skCircle(sketch, "E242", {"center": v(-65, 65) * mm, "radius": 63.25 * mm, "construction": true});
            skCircle(sketch, "E243", {"center": v(65, 65) * mm, "radius": 63.25 * mm, "construction": true});
            skCircle(sketch, "E244", {"center": v(-65, -65) * mm, "radius": 63.25 * mm, "construction": true});
            skPoint(sketch, "E245.second.point", {"position": v(-109.7, 103.75) * mm});
            skPoint(sketch, "E245.third.point", {"position": v(-103.7, 108.66) * mm});
            skPoint(sketch, "E246.second.point", {"position": v(103.75, 109.7) * mm});
            skPoint(sketch, "E246.third.point", {"position": v(109.03, 103.75) * mm});
            skPoint(sketch, "E246.third.point.positionSnap0", {"position": v(109.7, 103.75) * mm});
            skPoint(sketch, "E247.second.point", {"position": v(109.7, -103.75) * mm});
            skPoint(sketch, "E247.third.point", {"position": v(103.76, -109.16) * mm});
            skPoint(sketch, "E248.second.point", {"position": v(-109.7, -103.75) * mm});
            skPoint(sketch, "E248.third.point", {"position": v(-103.75, -109.03) * mm});
            skPoint(sketch, "E248.third.point.positionSnap0", {"position": v(-103.75, -109.7) * mm});
            skCircle(sketch, "E249", {"center": v(-108.3, 108.15) * mm, "radius": 1.55 * mm});
            skCircle(sketch, "E250", {"center": v(-48.74, 126.12) * mm, "radius": 1.55 * mm});
            skCircle(sketch, "E251", {"center": v(-126.12, 48.74) * mm, "radius": 1.55 * mm});
            skCircle(sketch, "E252", {"center": v(-126.12, -48.74) * mm, "radius": 1.55 * mm});
            skCircle(sketch, "E253", {"center": v(-108.3, -108.15) * mm, "radius": 1.55 * mm});
            skCircle(sketch, "E254", {"center": v(-48.74, -126.12) * mm, "radius": 1.55 * mm});
            skCircle(sketch, "E255", {"center": v(48.74, -126.12) * mm, "radius": 1.55 * mm});
            skCircle(sketch, "E256", {"center": v(108.28, -108.16) * mm, "radius": 1.55 * mm});
            skCircle(sketch, "E257", {"center": v(126.12, -48.74) * mm, "radius": 1.55 * mm});
            skCircle(sketch, "E258", {"center": v(126.12, 48.74) * mm, "radius": 1.55 * mm});
            skCircle(sketch, "E259", {"center": v(108.15, 108.3) * mm, "radius": 1.55 * mm});
            skCircle(sketch, "E260", {"center": v(48.74, 126.12) * mm, "radius": 1.55 * mm});
            skCircle(sketch, "E261", {"center": v(0, 79.89) * mm, "radius": 1.55 * mm});
            skCircle(sketch, "E262", {"center": v(-79.89, 0) * mm, "radius": 1.55 * mm});
            skCircle(sketch, "E263.MirrorC", {"center": v(0, -79.89) * mm, "radius": 1.55 * mm});
            skCircle(sketch, "E264.MirrorC", {"center": v(79.89, 0) * mm, "radius": 1.55 * mm});
            skSolve(sketch);
        }
        {
            var Q0;
            {var subQ3=sQuery(id+"F0.wireOp",EDGE,"E10");Q0=makeQuery(id+"F0.imprint","IMPRINT",FACE,{"disambiguationData":[TD([[makeQuery(id+"F0.imprint","IMPRINT",EDGE,{"derivedFrom":subQ3}),1.0]])]});}
            var Q1;
            {var subQ0=sQuery(id+"F0.wireOp",EDGE,"E21.0.startCap");Q1=makeQuery(id+"F0.imprint","IMPRINT",FACE,{"disambiguationData":[TD([[makeQuery(id+"F0.imprint","IMPRINT",EDGE,{"derivedFrom":subQ0}),1.0]])]});}
            var Q2;
            {var subQ3=sQuery(id+"F0.wireOp",EDGE,"E21.0.endCap");Q2=makeQuery(id+"F0.imprint","IMPRINT",FACE,{"disambiguationData":[TD([[makeQuery(id+"F0.imprint","IMPRINT",EDGE,{"derivedFrom":subQ3}),1.0]])]});}
            var Q3;
            {var subQ3=sQuery(id+"F0.wireOp",EDGE,"E21.0.endCap");Q3=makeQuery(id+"F0.imprint","IMPRINT",FACE,{"disambiguationData":[TD([[makeQuery(id+"F0.imprint","IMPRINT",EDGE,{"derivedFrom":subQ3}),-1.0]])]});}
            var Q4;
            {var subQ3=sQuery(id+"F0.wireOp",EDGE,"E21.0.startCap");Q4=makeQuery(id+"F0.imprint","IMPRINT",FACE,{"disambiguationData":[TD([[makeQuery(id+"F0.imprint","IMPRINT",EDGE,{"derivedFrom":subQ3}),-1.0]])]});}
            var Q5;
            {var subQ3=sQuery(id+"F0.wireOp",EDGE,"E22.0.startCap");Q5=makeQuery(id+"F0.imprint","IMPRINT",FACE,{"disambiguationData":[TD([[makeQuery(id+"F0.imprint","IMPRINT",EDGE,{"derivedFrom":subQ3}),-1.0]])]});}
            var Q6;
            {var subQ1=sQuery(id+"F0.wireOp",EDGE,"E22.1.endCap");Q6=makeQuery(id+"F0.imprint","IMPRINT",FACE,{"disambiguationData":[TD([[makeQuery(id+"F0.imprint","IMPRINT",EDGE,{"derivedFrom":subQ1}),1.0]])]});}
            var Q7;
            {var subQ1=sQuery(id+"F0.wireOp",EDGE,"E22.1.endCap");Q7=makeQuery(id+"F0.imprint","IMPRINT",FACE,{"disambiguationData":[TD([[makeQuery(id+"F0.imprint","IMPRINT",EDGE,{"derivedFrom":subQ1}),-1.0]])]});}
            var Q8;
            {var subQ4=sQuery(id+"F0.wireOp",EDGE,"E22.0.startCap");Q8=makeQuery(id+"F0.imprint","IMPRINT",FACE,{"disambiguationData":[TD([[makeQuery(id+"F0.imprint","IMPRINT",EDGE,{"derivedFrom":subQ4}),1.0]])]});}
            var Q9;
            {var subQ1=sQuery(id+"F0.wireOp",EDGE,"E9.rect.left");var subQ8=sQuery(id+"F0.wireOp",EDGE,"E9.rect.bottom");var subQ9=makeQuery(id+"F0.imprint","INTERSECT",VERTEX,{"derivedFrom":[subQ8,subQ1]});Q9=makeQuery(id+"F0.imprint","IMPRINT",FACE,{"disambiguationData":[TD([[makeQuery(id+"F0.imprint","IMPRINT",EDGE,{"disambiguationData":[TD([[subQ9,-1.0]])],"derivedFrom":subQ8}),-1.0]])]});}
            extrude(context, id + "F1", {"entities" : qUnion([Q0, Q1, Q2, Q3, Q4, Q5, Q6, Q7, Q8, Q9]), "depth" : 3 * mm});
        }
        {
            var Q0;
            Q0=makeQuery(id+"F1.opExtrude","CAP_FACE",FACE,{"disambiguationData":[OSD([sQuery(id+"F0.wireOp",EDGE,"E5"),sQuery(id+"F0.wireOp",EDGE,"E6"),sQuery(id+"F0.wireOp",EDGE,"E7"),sQuery(id+"F0.wireOp",EDGE,"E8"),sQuery(id+"F0.wireOp",EDGE,"E10"),sQuery(id+"F0.wireOp",EDGE,"E11"),sQuery(id+"F0.wireOp",EDGE,"E12"),sQuery(id+"F0.wireOp",EDGE,"E13"),sQuery(id+"F0.wireOp",EDGE,"E15"),sQuery(id+"F0.wireOp",EDGE,"E16"),sQuery(id+"F0.wireOp",EDGE,"E17"),sQuery(id+"F0.wireOp",EDGE,"E18"),sQuery(id+"F0.wireOp",EDGE,"E19.0"),sQuery(id+"F0.wireOp",EDGE,"E20.0"),sQuery(id+"F0.wireOp",EDGE,"E21.0.left"),sQuery(id+"F0.wireOp",EDGE,"E22.1.right"),sQuery(id+"F0.wireOp",EDGE,"E23.0.right"),sQuery(id+"F0.wireOp",EDGE,"E24.trimOffspring"),sQuery(id+"F0.wireOp",EDGE,"E25.trimOffspring"),sQuery(id+"F0.wireOp",EDGE,"E26.trimOffspring"),sQuery(id+"F0.wireOp",EDGE,"E27.trimOffspring"),sQuery(id+"F0.wireOp",EDGE,"E28.trimOffspring"),sQuery(id+"F0.wireOp",EDGE,"E29.trimOffspring"),sQuery(id+"F0.wireOp",EDGE,"E30.trimOffspring"),sQuery(id+"F0.wireOp",EDGE,"E31.filletArc"),sQuery(id+"F0.wireOp",EDGE,"E32.filletArc"),sQuery(id+"F0.wireOp",EDGE,"E33.filletArc"),sQuery(id+"F0.wireOp",EDGE,"E34.filletArc"),sQuery(id+"F0.wireOp",EDGE,"E35.trimOffspring"),sQuery(id+"F0.wireOp",EDGE,"E36.trimOffspring"),sQuery(id+"F0.wireOp",EDGE,"E37.trimOffspring"),sQuery(id+"F0.wireOp",EDGE,"E38.trimOffspring"),sQuery(id+"F0.wireOp",EDGE,"E39.filletArc"),sQuery(id+"F0.wireOp",EDGE,"E40.filletArc"),sQuery(id+"F0.wireOp",EDGE,"E41.filletArc"),sQuery(id+"F0.wireOp",EDGE,"E42.filletArc"),sQuery(id+"F0.wireOp",EDGE,"E43.filletArc"),sQuery(id+"F0.wireOp",EDGE,"E44.filletArc"),sQuery(id+"F0.wireOp",EDGE,"E45.filletArc"),sQuery(id+"F0.wireOp",EDGE,"E46.filletArc"),sQuery(id+"F0.wireOp",EDGE,"E13"),sQuery(id+"F0.wireOp",EDGE,"E11"),sQuery(id+"F0.wireOp",EDGE,"E13"),sQuery(id+"F0.wireOp",EDGE,"E47.filletArc"),sQuery(id+"F0.wireOp",EDGE,"E48.filletArc"),sQuery(id+"F0.wireOp",EDGE,"E10"),sQuery(id+"F0.wireOp",EDGE,"E11"),sQuery(id+"F0.wireOp",EDGE,"E12"),sQuery(id+"F0.wireOp",EDGE,"E12"),sQuery(id+"F0.wireOp",EDGE,"E10"),sQuery(id+"F0.wireOp",EDGE,"E49.filletArc"),sQuery(id+"F0.wireOp",EDGE,"E50.filletArc"),sQuery(id+"F0.wireOp",EDGE,"E51.filletArc"),sQuery(id+"F0.wireOp",EDGE,"E52.filletArc"),sQuery(id+"F0.wireOp",EDGE,"E53.filletArc"),sQuery(id+"F0.wireOp",EDGE,"E54.filletArc"),sQuery(id+"F0.wireOp",EDGE,"E55.filletArc"),sQuery(id+"F0.wireOp",EDGE,"E56.filletArc"),sQuery(id+"F0.wireOp",EDGE,"E57.filletArc"),sQuery(id+"F0.wireOp",EDGE,"E58.filletArc"),sQuery(id+"F0.wireOp",EDGE,"E59.filletArc"),sQuery(id+"F0.wireOp",EDGE,"E60.filletArc"),sQuery(id+"F0.wireOp",EDGE,"E61.filletArc"),sQuery(id+"F0.wireOp",EDGE,"E62.filletArc"),sQuery(id+"F0.wireOp",EDGE,"E67.0.left"),sQuery(id+"F0.wireOp",EDGE,"E67.0.right"),sQuery(id+"F0.wireOp",EDGE,"E67.1.left"),sQuery(id+"F0.wireOp",EDGE,"E67.1.right"),sQuery(id+"F0.wireOp",EDGE,"E67.2.left"),sQuery(id+"F0.wireOp",EDGE,"E67.2.right"),sQuery(id+"F0.wireOp",EDGE,"E67.3.left"),sQuery(id+"F0.wireOp",EDGE,"E67.3.right"),sQuery(id+"F0.wireOp",EDGE,"E70.trimOffspring"),sQuery(id+"F0.wireOp",EDGE,"E73.trimOffspring"),sQuery(id+"F0.wireOp",EDGE,"E76.trimOffspring"),sQuery(id+"F0.wireOp",EDGE,"E77.trimOffspring"),sQuery(id+"F0.wireOp",EDGE,"E80.filletArc"),sQuery(id+"F0.wireOp",EDGE,"E81.filletArc"),sQuery(id+"F0.wireOp",EDGE,"E82.filletArc"),sQuery(id+"F0.wireOp",EDGE,"E83.filletArc"),sQuery(id+"F0.wireOp",EDGE,"E84.filletArc"),sQuery(id+"F0.wireOp",EDGE,"E85.filletArc"),sQuery(id+"F0.wireOp",EDGE,"E86.filletArc"),sQuery(id+"F0.wireOp",EDGE,"E87.filletArc"),sQuery(id+"F0.wireOp",EDGE,"E88.filletArc"),sQuery(id+"F0.wireOp",EDGE,"E89.filletArc"),sQuery(id+"F0.wireOp",EDGE,"E90.filletArc"),sQuery(id+"F0.wireOp",EDGE,"E91.filletArc"),sQuery(id+"F0.wireOp",EDGE,"E92.filletArc"),sQuery(id+"F0.wireOp",EDGE,"E93.filletArc"),sQuery(id+"F0.wireOp",EDGE,"E94.filletArc"),sQuery(id+"F0.wireOp",EDGE,"E95.filletArc"),sQuery(id+"F0.wireOp",EDGE,"E96"),sQuery(id+"F0.wireOp",EDGE,"E97"),sQuery(id+"F0.wireOp",EDGE,"E98"),sQuery(id+"F0.wireOp",EDGE,"E99"),sQuery(id+"F0.wireOp",EDGE,"E100"),sQuery(id+"F0.wireOp",EDGE,"E101"),sQuery(id+"F0.wireOp",EDGE,"E102"),sQuery(id+"F0.wireOp",EDGE,"E103"),sQuery(id+"F0.wireOp",EDGE,"E104"),sQuery(id+"F0.wireOp",EDGE,"E105"),sQuery(id+"F0.wireOp",EDGE,"E106"),sQuery(id+"F0.wireOp",EDGE,"E107"),sQuery(id+"F0.wireOp",EDGE,"E112.0.startCap"),sQuery(id+"F0.wireOp",EDGE,"E112.0.endCap"),sQuery(id+"F0.wireOp",EDGE,"E112.0.left"),sQuery(id+"F0.wireOp",EDGE,"E112.0.right"),sQuery(id+"F0.wireOp",EDGE,"E113.0.startCap"),sQuery(id+"F0.wireOp",EDGE,"E113.0.endCap"),sQuery(id+"F0.wireOp",EDGE,"E113.0.left"),sQuery(id+"F0.wireOp",EDGE,"E113.0.right"),sQuery(id+"F0.wireOp",EDGE,"E114.0.startCap"),sQuery(id+"F0.wireOp",EDGE,"E114.0.endCap"),sQuery(id+"F0.wireOp",EDGE,"E114.0.left"),sQuery(id+"F0.wireOp",EDGE,"E114.0.right"),sQuery(id+"F0.wireOp",EDGE,"E115.0.startCap"),sQuery(id+"F0.wireOp",EDGE,"E115.0.endCap"),sQuery(id+"F0.wireOp",EDGE,"E115.0.left"),sQuery(id+"F0.wireOp",EDGE,"E115.0.right"),sQuery(id+"F0.wireOp",EDGE,"E117.MirrorCS"),sQuery(id+"F0.wireOp",EDGE,"E118.MirrorCS"),sQuery(id+"F0.wireOp",EDGE,"E119.MirrorCS"),sQuery(id+"F0.wireOp",EDGE,"E120.MirrorCS"),sQuery(id+"F0.wireOp",EDGE,"E122.MirrorCS"),sQuery(id+"F0.wireOp",EDGE,"E123.MirrorCS"),sQuery(id+"F0.wireOp",EDGE,"E124.MirrorCS"),sQuery(id+"F0.wireOp",EDGE,"E126.MirrorCS"),sQuery(id+"F0.wireOp",EDGE,"E127.MirrorCS"),sQuery(id+"F0.wireOp",EDGE,"E128.MirrorCS"),sQuery(id+"F0.wireOp",EDGE,"E129.MirrorCS"),sQuery(id+"F0.wireOp",EDGE,"E130.MirrorCS"),sQuery(id+"F0.wireOp",EDGE,"E131.MirrorCS"),sQuery(id+"F0.wireOp",EDGE,"E132.MirrorCS"),sQuery(id+"F0.wireOp",EDGE,"E133.MirrorCS"),sQuery(id+"F0.wireOp",EDGE,"E134"),sQuery(id+"F0.wireOp",EDGE,"E136.MirrorCS"),sQuery(id+"F0.wireOp",EDGE,"E137.MirrorCS"),sQuery(id+"F0.wireOp",EDGE,"E138.MirrorCS"),sQuery(id+"F0.wireOp",EDGE,"E140.MirrorCS"),sQuery(id+"F0.wireOp",EDGE,"E141.MirrorCS"),sQuery(id+"F0.wireOp",EDGE,"E143.MirrorCS"),sQuery(id+"F0.wireOp",EDGE,"E144.MirrorCS"),sQuery(id+"F0.wireOp",EDGE,"E145.MirrorCS"),sQuery(id+"F0.wireOp",EDGE,"E146.MirrorCS"),sQuery(id+"F0.wireOp",EDGE,"E147.MirrorCS"),sQuery(id+"F0.wireOp",EDGE,"E148.MirrorCS"),sQuery(id+"F0.wireOp",EDGE,"E149.MirrorCS"),sQuery(id+"F0.wireOp",EDGE,"E150.MirrorCS"),sQuery(id+"F0.wireOp",EDGE,"E151.MirrorCS"),sQuery(id+"F0.wireOp",EDGE,"E152.MirrorCS"),sQuery(id+"F0.wireOp",EDGE,"E153.MirrorCS"),sQuery(id+"F0.wireOp",EDGE,"E155.MirrorCS"),sQuery(id+"F0.wireOp",EDGE,"E156.MirrorCS"),sQuery(id+"F0.wireOp",EDGE,"E157.MirrorCS"),sQuery(id+"F0.wireOp",EDGE,"E158.MirrorCS"),sQuery(id+"F0.wireOp",EDGE,"E159.MirrorCS"),sQuery(id+"F0.wireOp",EDGE,"E161.MirrorCS"),sQuery(id+"F0.wireOp",EDGE,"E162.MirrorCS"),sQuery(id+"F0.wireOp",EDGE,"E163.MirrorCS"),sQuery(id+"F0.wireOp",EDGE,"E164.MirrorCS"),sQuery(id+"F0.wireOp",EDGE,"E165.MirrorCS"),sQuery(id+"F0.wireOp",EDGE,"E166.MirrorCS"),sQuery(id+"F0.wireOp",EDGE,"E168.MirrorCS"),sQuery(id+"F0.wireOp",EDGE,"E169.MirrorCS"),sQuery(id+"F0.wireOp",EDGE,"E171.MirrorCS"),sQuery(id+"F0.wireOp",EDGE,"E172.MirrorCS"),sQuery(id+"F0.wireOp",EDGE,"E173.MirrorCS"),sQuery(id+"F0.wireOp",EDGE,"E177.MirrorC"),sQuery(id+"F0.wireOp",EDGE,"E178.MirrorC"),sQuery(id+"F0.wireOp",EDGE,"E179.MirrorC"),sQuery(id+"F0.wireOp",EDGE,"E180.MirrorC"),sQuery(id+"F0.wireOp",EDGE,"E181.MirrorC"),sQuery(id+"F0.wireOp",EDGE,"E182.MirrorC"),sQuery(id+"F0.wireOp",EDGE,"E183.MirrorC"),sQuery(id+"F0.wireOp",EDGE,"E184.trimOffspring"),sQuery(id+"F0.wireOp",EDGE,"E185.trimOffspring"),sQuery(id+"F0.wireOp",EDGE,"E186.trimOffspring"),sQuery(id+"F0.wireOp",EDGE,"E187.trimOffspring"),sQuery(id+"F0.wireOp",EDGE,"E188.trimOffspring"),sQuery(id+"F0.wireOp",EDGE,"E189.trimOffspring"),sQuery(id+"F0.wireOp",EDGE,"E191.trimOffspring"),sQuery(id+"F0.wireOp",EDGE,"E192.trimOffspring"),sQuery(id+"F0.wireOp",EDGE,"E193.trimOffspring"),sQuery(id+"F0.wireOp",EDGE,"E194.trimOffspring"),sQuery(id+"F0.wireOp",EDGE,"E195.trimOffspring"),sQuery(id+"F0.wireOp",EDGE,"E196.trimOffspring"),sQuery(id+"F0.wireOp",EDGE,"E197.trimOffspring"),sQuery(id+"F0.wireOp",EDGE,"E198.trimOffspring"),sQuery(id+"F0.wireOp",EDGE,"E199.trimOffspring"),sQuery(id+"F0.wireOp",EDGE,"E200.trimOffspring"),sQuery(id+"F0.wireOp",EDGE,"E201.trimOffspring"),sQuery(id+"F0.wireOp",EDGE,"E202.trimOffspring"),sQuery(id+"F0.wireOp",EDGE,"E203.trimOffspring"),sQuery(id+"F0.wireOp",EDGE,"E204.trimOffspring"),sQuery(id+"F0.wireOp",EDGE,"E205.trimOffspring"),sQuery(id+"F0.wireOp",EDGE,"E206.trimOffspring"),sQuery(id+"F0.wireOp",EDGE,"E207.trimOffspring"),sQuery(id+"F0.wireOp",EDGE,"E208.trimOffspring"),sQuery(id+"F0.wireOp",EDGE,"E209.filletArc"),sQuery(id+"F0.wireOp",EDGE,"E210.filletArc"),sQuery(id+"F0.wireOp",EDGE,"E211.filletArc"),sQuery(id+"F0.wireOp",EDGE,"E212.filletArc"),sQuery(id+"F0.wireOp",EDGE,"E213.filletArc"),sQuery(id+"F0.wireOp",EDGE,"E214.filletArc"),sQuery(id+"F0.wireOp",EDGE,"E215.filletArc"),sQuery(id+"F0.wireOp",EDGE,"E216.filletArc"),sQuery(id+"F0.wireOp",EDGE,"E217.filletArc"),sQuery(id+"F0.wireOp",EDGE,"E218.filletArc"),sQuery(id+"F0.wireOp",EDGE,"E219.filletArc"),sQuery(id+"F0.wireOp",EDGE,"E220.filletArc"),sQuery(id+"F0.wireOp",EDGE,"E221.filletArc"),sQuery(id+"F0.wireOp",EDGE,"E222.filletArc"),sQuery(id+"F0.wireOp",EDGE,"E223.filletArc"),sQuery(id+"F0.wireOp",EDGE,"E224.filletArc"),sQuery(id+"F0.wireOp",EDGE,"E225.trimOffspring"),sQuery(id+"F0.wireOp",EDGE,"E226.filletArc"),sQuery(id+"F0.wireOp",EDGE,"E227.filletArc"),sQuery(id+"F0.wireOp",EDGE,"E228.filletArc"),sQuery(id+"F0.wireOp",EDGE,"E229.filletArc"),sQuery(id+"F0.wireOp",EDGE,"E230.filletArc"),sQuery(id+"F0.wireOp",EDGE,"E231.filletArc"),sQuery(id+"F0.wireOp",EDGE,"E232.filletArc"),sQuery(id+"F0.wireOp",EDGE,"E233.filletArc"),sQuery(id+"F0.wireOp",EDGE,"E234.filletArc"),sQuery(id+"F0.wireOp",EDGE,"E235.filletArc"),sQuery(id+"F0.wireOp",EDGE,"E236.filletArc"),sQuery(id+"F0.wireOp",EDGE,"E237.filletArc"),sQuery(id+"F0.wireOp",EDGE,"E238.filletArc"),sQuery(id+"F0.wireOp",EDGE,"E239.filletArc"),sQuery(id+"F0.wireOp",EDGE,"E240.filletArc"),sQuery(id+"F0.wireOp",EDGE,"E241.filletArc"),sQuery(id+"F0.wireOp",EDGE,"E249"),sQuery(id+"F0.wireOp",EDGE,"E250"),sQuery(id+"F0.wireOp",EDGE,"E251"),sQuery(id+"F0.wireOp",EDGE,"E252"),sQuery(id+"F0.wireOp",EDGE,"E253"),sQuery(id+"F0.wireOp",EDGE,"E254"),sQuery(id+"F0.wireOp",EDGE,"E255"),sQuery(id+"F0.wireOp",EDGE,"E256"),sQuery(id+"F0.wireOp",EDGE,"E257"),sQuery(id+"F0.wireOp",EDGE,"E258"),sQuery(id+"F0.wireOp",EDGE,"E259"),sQuery(id+"F0.wireOp",EDGE,"E260"),sQuery(id+"F0.wireOp",EDGE,"E261"),sQuery(id+"F0.wireOp",EDGE,"E262"),sQuery(id+"F0.wireOp",EDGE,"E263.MirrorC"),sQuery(id+"F0.wireOp",EDGE,"E264.MirrorC")])],"isStart":false});
            var sketch = newSketch(context, id + "F2", { "sketchPlane" : qUnion([Q0])});
            skLineSegment(sketch, "E265.rect.left", {"start": v(29, -37.5) * mm, "end": v(29, -12.88) * mm});
            skLineSegment(sketch, "E265.rect.right", {"start": v(-29, -37.5) * mm, "end": v(-29, -12.67) * mm});
            skPoint(sketch, "E265.rect.middle", {"position": v(0, 0) * mm});
            skPoint(sketch, "E266.visualSharp", {"position": v(-29, 42.5) * mm});
            skArc(sketch, "E266.filletArc", {"start": v(-24, 61.6) * mm, "mid": v(-27.54, 60.14) * mm, "end": v(-29, 56.6) * mm});
            skPoint(sketch, "E267.visualSharp", {"position": v(29, 42.5) * mm});
            skArc(sketch, "E267.filletArc", {"start": v(29, 56.98) * mm, "mid": v(27.54, 60.51) * mm, "end": v(24, 61.98) * mm});
            skPoint(sketch, "E268.visualSharp", {"position": v(29, -42.5) * mm});
            skArc(sketch, "E268.filletArc", {"start": v(24, -42.5) * mm, "mid": v(27.54, -41.04) * mm, "end": v(29, -37.5) * mm});
            skPoint(sketch, "E269.visualSharp", {"position": v(-29, -42.5) * mm});
            skArc(sketch, "E269.filletArc", {"start": v(-29, -37.5) * mm, "mid": v(-27.54, -41.04) * mm, "end": v(-24, -42.5) * mm});
            skArc(sketch, "E270", {"start": v(-28.46, -10.41) * mm, "mid": v(-26.11, -0.53) * mm, "end": v(-28.46, 9.35) * mm});
            skArc(sketch, "E271", {"start": v(28.44, 9.67) * mm, "mid": v(25.96, -0.45) * mm, "end": v(28.44, -10.57) * mm});
            skLineSegment(sketch, "E272.trimOffspring", {"start": v(-29, 11.6) * mm, "end": v(-29, 56.6) * mm});
            skLineSegment(sketch, "E273.trimOffspring", {"start": v(29, 11.98) * mm, "end": v(29, 56.98) * mm});
            skPoint(sketch, "E274.visualSharp", {"position": v(-29, 10.35) * mm});
            skArc(sketch, "E274.filletArc", {"start": v(-29, 11.6) * mm, "mid": v(-28.86, 10.45) * mm, "end": v(-28.46, 9.35) * mm});
            skPoint(sketch, "E275.visualSharp", {"position": v(-29, -11.41) * mm});
            skArc(sketch, "E275.filletArc", {"start": v(-28.46, -10.41) * mm, "mid": v(-28.86, -11.5) * mm, "end": v(-29, -12.67) * mm});
            skPoint(sketch, "E276.visualSharp", {"position": v(29, 10.69) * mm});
            skArc(sketch, "E276.filletArc", {"start": v(28.44, 9.67) * mm, "mid": v(28.86, 10.79) * mm, "end": v(29, 11.98) * mm});
            skPoint(sketch, "E277.visualSharp", {"position": v(29, -11.59) * mm});
            skArc(sketch, "E277.filletArc", {"start": v(29, -12.88) * mm, "mid": v(28.86, -11.69) * mm, "end": v(28.44, -10.57) * mm});
            skCircle(sketch, "E278", {"center": v(-26, 26) * mm, "radius": 1.55 * mm});
            skCircle(sketch, "E279", {"center": v(26, 26) * mm, "radius": 1.55 * mm});
            skCircle(sketch, "E280", {"center": v(-26, -26) * mm, "radius": 1.55 * mm});
            skCircle(sketch, "E281", {"center": v(26, -26) * mm, "radius": 1.55 * mm});
            skArc(sketch, "E282", {"start": v(24, 61.98) * mm, "mid": v(-0.02, 64.24) * mm, "end": v(-24, 61.6) * mm});
            skArc(sketch, "E283", {"start": v(-24, -42.5) * mm, "mid": v(0, -45.55) * mm, "end": v(24, -42.5) * mm});
            skPoint(sketch, "E284.MirrorCS.end.orphan", {"position": v(-24, -61.6) * mm});
            skPoint(sketch, "E284.MirrorCS.start.orphan", {"position": v(24, -61.98) * mm});
            skSolve(sketch);
        }
        {
            var Q0;
            Q0 = qSketchRegion(id + "F2", true);
            extrude(context, id + "F3", {"entities" : qUnion([Q0]), "depth" : 2 * mm});
        }
        {
            var Q0;
            Q0=makeQuery(id+"F3.opExtrude","CAP_FACE",FACE,{"disambiguationData":[OSD([sQuery(id+"F2.wireOp",EDGE,"E265.rect.left"),sQuery(id+"F2.wireOp",EDGE,"E265.rect.right"),sQuery(id+"F2.wireOp",EDGE,"E266.filletArc"),sQuery(id+"F2.wireOp",EDGE,"E267.filletArc"),sQuery(id+"F2.wireOp",EDGE,"E268.filletArc"),sQuery(id+"F2.wireOp",EDGE,"E269.filletArc"),sQuery(id+"F2.wireOp",EDGE,"E270"),sQuery(id+"F2.wireOp",EDGE,"E271"),sQuery(id+"F2.wireOp",EDGE,"E272.trimOffspring"),sQuery(id+"F2.wireOp",EDGE,"E273.trimOffspring"),sQuery(id+"F2.wireOp",EDGE,"E274.filletArc"),sQuery(id+"F2.wireOp",EDGE,"E275.filletArc"),sQuery(id+"F2.wireOp",EDGE,"E276.filletArc"),sQuery(id+"F2.wireOp",EDGE,"E277.filletArc"),sQuery(id+"F2.wireOp",EDGE,"E278"),sQuery(id+"F2.wireOp",EDGE,"E279"),sQuery(id+"F2.wireOp",EDGE,"E280"),sQuery(id+"F2.wireOp",EDGE,"E281"),sQuery(id+"F2.wireOp",EDGE,"E282"),sQuery(id+"F2.wireOp",EDGE,"E284.MirrorCS")])],"isStart":false});
            var sketch = newSketch(context, id + "F4", { "sketchPlane" : qUnion([Q0])});
            skArc(sketch, "E285.0.startCap", {"start": v(-20.75, -12) * mm, "mid": v(-21.5, -12.75) * mm, "end": v(-22.25, -12) * mm});
            skLineSegment(sketch, "E285.0.left", {"start": v(-22.25, -12) * mm, "end": v(-22.25, 12) * mm});
            skLineSegment(sketch, "E285.0.right", {"start": v(-20.75, -12) * mm, "end": v(-20.75, 12) * mm});
            skLineSegment(sketch, "E286.MirrorCS", {"start": v(20.75, -12) * mm, "end": v(20.75, 12) * mm});
            skLineSegment(sketch, "E287.MirrorCS", {"start": v(22.25, -12) * mm, "end": v(22.25, 12) * mm});
            skArc(sketch, "E288.MirrorCS", {"start": v(20.75, -12) * mm, "mid": v(21.5, -12.75) * mm, "end": v(22.25, -12) * mm});
            skPoint(sketch, "E289.rect.left.end.orphan", {"position": v(21.5, 12) * mm});
            skPoint(sketch, "E290.startSnap0", {"position": v(20.46, 53.44) * mm});
            skLineSegment(sketch, "E291.2.0.8", {"start": v(24.22, -8.23) * mm, "end": v(24.28, -40.72) * mm, "construction": true});
            skLineSegment(sketch, "E292.MirrorCS", {"start": v(24.17, 23.98) * mm, "end": v(24.22, -8.52) * mm, "construction": true});
            skLineSegment(sketch, "E293.MirrorCS", {"start": v(24.17, 8.58) * mm, "end": v(24.22, -8.52) * mm});
            skLineSegment(sketch, "E294", {"start": v(-15.3, 2.75) * mm, "end": v(15.29, 2.75) * mm});
            skLineSegment(sketch, "E295", {"start": v(-15.3, 8.25) * mm, "end": v(15.29, 8.25) * mm});
            skLineSegment(sketch, "E296", {"start": v(-15.3, 13.75) * mm, "end": v(15.29, 13.75) * mm});
            skLineSegment(sketch, "E297", {"start": v(-15.3, 19.25) * mm, "end": v(15.29, 19.25) * mm});
            skLineSegment(sketch, "E298", {"start": v(-15.3, 24.75) * mm, "end": v(15.29, 24.75) * mm});
            skLineSegment(sketch, "E299", {"start": v(-15.3, 30.25) * mm, "end": v(15.29, 30.25) * mm});
            skLineSegment(sketch, "E300", {"start": v(-15.3, 35.75) * mm, "end": v(15.29, 35.75) * mm});
            skLineSegment(sketch, "E301.MirrorCS", {"start": v(-15.3, -24.75) * mm, "end": v(15.29, -24.75) * mm});
            skLineSegment(sketch, "E302.MirrorCS", {"start": v(-15.3, -19.25) * mm, "end": v(15.29, -19.25) * mm});
            skLineSegment(sketch, "E303.MirrorCS", {"start": v(-15.3, -13.75) * mm, "end": v(15.29, -13.75) * mm});
            skLineSegment(sketch, "E304.MirrorCS", {"start": v(-15.3, -35.75) * mm, "end": v(15.29, -35.75) * mm});
            skLineSegment(sketch, "E305.MirrorCS", {"start": v(-15.3, -2.75) * mm, "end": v(15.29, -2.75) * mm});
            skLineSegment(sketch, "E306.MirrorCS", {"start": v(-15.3, -30.25) * mm, "end": v(15.29, -30.25) * mm});
            skLineSegment(sketch, "E307.MirrorCS", {"start": v(-15.3, -8.25) * mm, "end": v(15.29, -8.25) * mm});
            skArc(sketch, "E308.0.startCap", {"start": v(-15.3, 34.25) * mm, "mid": v(-16.8, 35.75) * mm, "end": v(-15.3, 37.25) * mm});
            skArc(sketch, "E308.0.endCap", {"start": v(15.29, 37.25) * mm, "mid": v(16.79, 35.75) * mm, "end": v(15.29, 34.25) * mm});
            skLineSegment(sketch, "E308.0.left", {"start": v(-15.3, 37.25) * mm, "end": v(15.29, 37.25) * mm});
            skLineSegment(sketch, "E308.0.right", {"start": v(-15.3, 34.25) * mm, "end": v(15.29, 34.25) * mm});
            skArc(sketch, "E308.1.startCap", {"start": v(-15.3, 28.75) * mm, "mid": v(-16.8, 30.25) * mm, "end": v(-15.3, 31.75) * mm});
            skArc(sketch, "E308.1.endCap", {"start": v(15.29, 31.75) * mm, "mid": v(16.79, 30.25) * mm, "end": v(15.29, 28.75) * mm});
            skLineSegment(sketch, "E308.1.left", {"start": v(-15.3, 31.75) * mm, "end": v(15.29, 31.75) * mm});
            skLineSegment(sketch, "E308.1.right", {"start": v(-15.3, 28.75) * mm, "end": v(15.29, 28.75) * mm});
            skArc(sketch, "E308.2.startCap", {"start": v(-15.3, 23.25) * mm, "mid": v(-16.8, 24.75) * mm, "end": v(-15.3, 26.25) * mm});
            skArc(sketch, "E308.2.endCap", {"start": v(15.29, 26.25) * mm, "mid": v(16.79, 24.75) * mm, "end": v(15.29, 23.25) * mm});
            skLineSegment(sketch, "E308.2.left", {"start": v(-15.3, 26.25) * mm, "end": v(15.29, 26.25) * mm});
            skLineSegment(sketch, "E308.2.right", {"start": v(-15.3, 23.25) * mm, "end": v(15.29, 23.25) * mm});
            skArc(sketch, "E308.3.startCap", {"start": v(-15.3, 17.75) * mm, "mid": v(-16.8, 19.25) * mm, "end": v(-15.3, 20.75) * mm});
            skArc(sketch, "E308.3.endCap", {"start": v(15.29, 20.75) * mm, "mid": v(16.79, 19.25) * mm, "end": v(15.29, 17.75) * mm});
            skLineSegment(sketch, "E308.3.left", {"start": v(-15.3, 20.75) * mm, "end": v(15.29, 20.75) * mm});
            skLineSegment(sketch, "E308.3.right", {"start": v(-15.3, 17.75) * mm, "end": v(15.29, 17.75) * mm});
            skArc(sketch, "E308.4.startCap", {"start": v(-15.3, 12.25) * mm, "mid": v(-16.8, 13.75) * mm, "end": v(-15.3, 15.25) * mm});
            skArc(sketch, "E308.4.endCap", {"start": v(15.29, 15.25) * mm, "mid": v(16.79, 13.75) * mm, "end": v(15.29, 12.25) * mm});
            skLineSegment(sketch, "E308.4.left", {"start": v(-15.3, 15.25) * mm, "end": v(15.29, 15.25) * mm});
            skLineSegment(sketch, "E308.4.right", {"start": v(-15.3, 12.25) * mm, "end": v(15.29, 12.25) * mm});
            skArc(sketch, "E308.5.startCap", {"start": v(-15.3, 6.75) * mm, "mid": v(-16.8, 8.25) * mm, "end": v(-15.3, 9.75) * mm});
            skArc(sketch, "E308.5.endCap", {"start": v(15.29, 9.75) * mm, "mid": v(16.79, 8.25) * mm, "end": v(15.29, 6.75) * mm});
            skLineSegment(sketch, "E308.5.left", {"start": v(-15.3, 9.75) * mm, "end": v(15.29, 9.75) * mm});
            skLineSegment(sketch, "E308.5.right", {"start": v(-15.3, 6.75) * mm, "end": v(15.29, 6.75) * mm});
            skArc(sketch, "E308.6.startCap", {"start": v(-15.3, 1.25) * mm, "mid": v(-16.8, 2.75) * mm, "end": v(-15.3, 4.25) * mm});
            skArc(sketch, "E308.6.endCap", {"start": v(15.29, 4.25) * mm, "mid": v(16.79, 2.75) * mm, "end": v(15.29, 1.25) * mm});
            skLineSegment(sketch, "E308.6.left", {"start": v(-15.3, 4.25) * mm, "end": v(15.29, 4.25) * mm});
            skLineSegment(sketch, "E308.6.right", {"start": v(-15.3, 1.25) * mm, "end": v(15.29, 1.25) * mm});
            skArc(sketch, "E308.7.startCap", {"start": v(-15.3, -4.25) * mm, "mid": v(-16.8, -2.75) * mm, "end": v(-15.3, -1.25) * mm});
            skArc(sketch, "E308.7.endCap", {"start": v(15.29, -1.25) * mm, "mid": v(16.79, -2.75) * mm, "end": v(15.29, -4.25) * mm});
            skLineSegment(sketch, "E308.7.left", {"start": v(-15.3, -1.25) * mm, "end": v(15.29, -1.25) * mm});
            skLineSegment(sketch, "E308.7.right", {"start": v(-15.3, -4.25) * mm, "end": v(15.29, -4.25) * mm});
            skArc(sketch, "E308.8.startCap", {"start": v(-15.3, -9.75) * mm, "mid": v(-16.8, -8.25) * mm, "end": v(-15.3, -6.75) * mm});
            skArc(sketch, "E308.8.endCap", {"start": v(15.29, -6.75) * mm, "mid": v(16.79, -8.25) * mm, "end": v(15.29, -9.75) * mm});
            skLineSegment(sketch, "E308.8.left", {"start": v(-15.3, -6.75) * mm, "end": v(15.29, -6.75) * mm});
            skLineSegment(sketch, "E308.8.right", {"start": v(-15.3, -9.75) * mm, "end": v(15.29, -9.75) * mm});
            skArc(sketch, "E308.9.startCap", {"start": v(-15.3, -15.25) * mm, "mid": v(-16.8, -13.75) * mm, "end": v(-15.3, -12.25) * mm});
            skArc(sketch, "E308.9.endCap", {"start": v(15.29, -12.25) * mm, "mid": v(16.79, -13.75) * mm, "end": v(15.29, -15.25) * mm});
            skLineSegment(sketch, "E308.9.left", {"start": v(-15.3, -12.25) * mm, "end": v(15.29, -12.25) * mm});
            skLineSegment(sketch, "E308.9.right", {"start": v(-15.3, -15.25) * mm, "end": v(15.29, -15.25) * mm});
            skArc(sketch, "E308.10.startCap", {"start": v(-15.3, -20.75) * mm, "mid": v(-16.8, -19.25) * mm, "end": v(-15.3, -17.75) * mm});
            skArc(sketch, "E308.10.endCap", {"start": v(15.29, -17.75) * mm, "mid": v(16.79, -19.25) * mm, "end": v(15.29, -20.75) * mm});
            skLineSegment(sketch, "E308.10.left", {"start": v(-15.3, -17.75) * mm, "end": v(15.29, -17.75) * mm});
            skLineSegment(sketch, "E308.10.right", {"start": v(-15.3, -20.75) * mm, "end": v(15.29, -20.75) * mm});
            skArc(sketch, "E308.11.startCap", {"start": v(-15.3, -26.25) * mm, "mid": v(-16.8, -24.75) * mm, "end": v(-15.3, -23.25) * mm});
            skArc(sketch, "E308.11.endCap", {"start": v(15.29, -23.25) * mm, "mid": v(16.79, -24.75) * mm, "end": v(15.29, -26.25) * mm});
            skLineSegment(sketch, "E308.11.left", {"start": v(-15.3, -23.25) * mm, "end": v(15.29, -23.25) * mm});
            skLineSegment(sketch, "E308.11.right", {"start": v(-15.3, -26.25) * mm, "end": v(15.29, -26.25) * mm});
            skArc(sketch, "E308.12.startCap", {"start": v(-15.3, -31.75) * mm, "mid": v(-16.8, -30.25) * mm, "end": v(-15.3, -28.75) * mm});
            skArc(sketch, "E308.12.endCap", {"start": v(15.29, -28.75) * mm, "mid": v(16.79, -30.25) * mm, "end": v(15.29, -31.75) * mm});
            skLineSegment(sketch, "E308.12.left", {"start": v(-15.3, -28.75) * mm, "end": v(15.29, -28.75) * mm});
            skLineSegment(sketch, "E308.12.right", {"start": v(-15.3, -31.75) * mm, "end": v(15.29, -31.75) * mm});
            skArc(sketch, "E308.13.startCap", {"start": v(-15.3, -37.25) * mm, "mid": v(-16.8, -35.75) * mm, "end": v(-15.3, -34.25) * mm});
            skArc(sketch, "E308.13.endCap", {"start": v(15.29, -34.25) * mm, "mid": v(16.79, -35.75) * mm, "end": v(15.29, -37.25) * mm});
            skLineSegment(sketch, "E308.13.left", {"start": v(-15.3, -34.25) * mm, "end": v(15.29, -34.25) * mm});
            skLineSegment(sketch, "E308.13.right", {"start": v(-15.3, -37.25) * mm, "end": v(15.29, -37.25) * mm});
            skLineSegment(sketch, "E309", {"start": v(-15.3, 41.25) * mm, "end": v(15.29, 41.25) * mm});
            skLineSegment(sketch, "E310", {"start": v(-15.3, 46.75) * mm, "end": v(15.29, 46.75) * mm});
            skLineSegment(sketch, "E311", {"start": v(-15.3, 52.25) * mm, "end": v(15.29, 52.25) * mm});
            skLineSegment(sketch, "E312", {"start": v(-15.3, 57.75) * mm, "end": v(15.29, 57.75) * mm});
            skPoint(sketch, "E313.end.orphan", {"position": v(15.29, 51.1) * mm});
            skPoint(sketch, "E313.start.orphan", {"position": v(-15.3, 51.1) * mm});
            skPoint(sketch, "E314.end.orphan", {"position": v(15.29, 54.3) * mm});
            skPoint(sketch, "E314.start.orphan", {"position": v(-15.3, 54.3) * mm});
            skLineSegment(sketch, "E315", {"start": v(-21.5, 12) * mm, "end": v(-21.5, 26.82) * mm});
            skLineSegment(sketch, "E316", {"start": v(21.5, 26.82) * mm, "end": v(21.5, 12) * mm});
            skArc(sketch, "E317.0.endCap", {"start": v(-22.25, 26.82) * mm, "mid": v(-21.5, 27.57) * mm, "end": v(-20.75, 26.82) * mm});
            skLineSegment(sketch, "E317.0.left", {"start": v(-22.25, 12) * mm, "end": v(-22.25, 26.82) * mm});
            skLineSegment(sketch, "E317.0.right", {"start": v(-20.75, 12) * mm, "end": v(-20.75, 26.82) * mm});
            skArc(sketch, "E318.0.startCap", {"start": v(20.75, 26.82) * mm, "mid": v(21.5, 27.57) * mm, "end": v(22.25, 26.82) * mm});
            skLineSegment(sketch, "E318.0.left", {"start": v(22.25, 26.82) * mm, "end": v(22.25, 12) * mm});
            skLineSegment(sketch, "E318.0.right", {"start": v(20.75, 26.82) * mm, "end": v(20.75, 12) * mm});
            skPoint(sketch, "E319.orphan", {"position": v(20.75, 12) * mm});
            skPoint(sketch, "E320.MirrorCS.start.orphan", {"position": v(22.25, 12) * mm});
            skArc(sketch, "E321.0.startCap", {"start": v(-15.3, 39.75) * mm, "mid": v(-16.8, 41.25) * mm, "end": v(-15.3, 42.75) * mm});
            skArc(sketch, "E321.0.endCap", {"start": v(15.29, 42.75) * mm, "mid": v(16.79, 41.25) * mm, "end": v(15.29, 39.75) * mm});
            skLineSegment(sketch, "E321.0.left", {"start": v(-15.3, 42.75) * mm, "end": v(15.29, 42.75) * mm});
            skLineSegment(sketch, "E321.0.right", {"start": v(-15.3, 39.75) * mm, "end": v(15.29, 39.75) * mm});
            skArc(sketch, "E322.0.startCap", {"start": v(-15.3, 45.25) * mm, "mid": v(-16.8, 46.75) * mm, "end": v(-15.3, 48.25) * mm});
            skArc(sketch, "E322.0.endCap", {"start": v(15.29, 48.25) * mm, "mid": v(16.79, 46.75) * mm, "end": v(15.29, 45.25) * mm});
            skLineSegment(sketch, "E322.0.left", {"start": v(-15.3, 48.25) * mm, "end": v(15.29, 48.25) * mm});
            skLineSegment(sketch, "E322.0.right", {"start": v(-15.3, 45.25) * mm, "end": v(15.29, 45.25) * mm});
            skArc(sketch, "E322.1.startCap", {"start": v(-15.3, 50.75) * mm, "mid": v(-16.8, 52.25) * mm, "end": v(-15.3, 53.75) * mm});
            skArc(sketch, "E322.1.endCap", {"start": v(15.29, 53.75) * mm, "mid": v(16.79, 52.25) * mm, "end": v(15.29, 50.75) * mm});
            skLineSegment(sketch, "E322.1.left", {"start": v(-15.3, 53.75) * mm, "end": v(15.29, 53.75) * mm});
            skLineSegment(sketch, "E322.1.right", {"start": v(-15.3, 50.75) * mm, "end": v(15.29, 50.75) * mm});
            skArc(sketch, "E322.2.startCap", {"start": v(-15.3, 56.25) * mm, "mid": v(-16.8, 57.75) * mm, "end": v(-15.3, 59.25) * mm});
            skArc(sketch, "E322.2.endCap", {"start": v(15.29, 59.25) * mm, "mid": v(16.79, 57.75) * mm, "end": v(15.29, 56.25) * mm});
            skLineSegment(sketch, "E322.2.left", {"start": v(-15.3, 59.25) * mm, "end": v(15.29, 59.25) * mm});
            skLineSegment(sketch, "E322.2.right", {"start": v(-15.3, 56.25) * mm, "end": v(15.29, 56.25) * mm});
            skSolve(sketch);
        }
        {
            var Q0;
            Q0=makeQuery(id+"F4.imprint","IMPRINT",FACE,{"disambiguationData":[TD([[makeQuery(id+"F4.imprint","IMPRINT",EDGE,{"derivedFrom":sQuery(id+"F4.wireOp",EDGE,"E308.0.startCap")}),-1.0]])]});
            var Q1;
            Q1=makeQuery(id+"F4.imprint","IMPRINT",FACE,{"disambiguationData":[TD([[makeQuery(id+"F4.imprint","IMPRINT",EDGE,{"derivedFrom":sQuery(id+"F4.wireOp",EDGE,"E308.1.startCap")}),-1.0]])]});
            var Q2;
            Q2=makeQuery(id+"F4.imprint","IMPRINT",FACE,{"disambiguationData":[TD([[makeQuery(id+"F4.imprint","IMPRINT",EDGE,{"derivedFrom":sQuery(id+"F4.wireOp",EDGE,"E308.2.startCap")}),-1.0]])]});
            var Q3;
            Q3=makeQuery(id+"F4.imprint","IMPRINT",FACE,{"disambiguationData":[TD([[makeQuery(id+"F4.imprint","IMPRINT",EDGE,{"derivedFrom":sQuery(id+"F4.wireOp",EDGE,"E308.3.startCap")}),-1.0]])]});
            var Q4;
            Q4=makeQuery(id+"F4.imprint","IMPRINT",FACE,{"disambiguationData":[TD([[makeQuery(id+"F4.imprint","IMPRINT",EDGE,{"derivedFrom":sQuery(id+"F4.wireOp",EDGE,"E308.4.startCap")}),-1.0]])]});
            var Q5;
            Q5=makeQuery(id+"F4.imprint","IMPRINT",FACE,{"disambiguationData":[TD([[makeQuery(id+"F4.imprint","IMPRINT",EDGE,{"derivedFrom":sQuery(id+"F4.wireOp",EDGE,"E308.5.startCap")}),-1.0]])]});
            var Q6;
            Q6=makeQuery(id+"F4.imprint","IMPRINT",FACE,{"disambiguationData":[TD([[makeQuery(id+"F4.imprint","IMPRINT",EDGE,{"derivedFrom":sQuery(id+"F4.wireOp",EDGE,"E308.6.startCap")}),-1.0]])]});
            var Q7;
            Q7=makeQuery(id+"F4.imprint","IMPRINT",FACE,{"disambiguationData":[TD([[makeQuery(id+"F4.imprint","IMPRINT",EDGE,{"derivedFrom":sQuery(id+"F4.wireOp",EDGE,"E308.7.startCap")}),-1.0]])]});
            var Q8;
            Q8=makeQuery(id+"F4.imprint","IMPRINT",FACE,{"disambiguationData":[TD([[makeQuery(id+"F4.imprint","IMPRINT",EDGE,{"derivedFrom":sQuery(id+"F4.wireOp",EDGE,"E308.8.startCap")}),-1.0]])]});
            var Q9;
            Q9=makeQuery(id+"F4.imprint","IMPRINT",FACE,{"disambiguationData":[TD([[makeQuery(id+"F4.imprint","IMPRINT",EDGE,{"derivedFrom":sQuery(id+"F4.wireOp",EDGE,"E308.9.startCap")}),-1.0]])]});
            var Q10;
            Q10=makeQuery(id+"F4.imprint","IMPRINT",FACE,{"disambiguationData":[TD([[makeQuery(id+"F4.imprint","IMPRINT",EDGE,{"derivedFrom":sQuery(id+"F4.wireOp",EDGE,"E308.10.startCap")}),-1.0]])]});
            var Q11;
            Q11=makeQuery(id+"F4.imprint","IMPRINT",FACE,{"disambiguationData":[TD([[makeQuery(id+"F4.imprint","IMPRINT",EDGE,{"derivedFrom":sQuery(id+"F4.wireOp",EDGE,"E308.11.startCap")}),-1.0]])]});
            var Q12;
            Q12=makeQuery(id+"F4.imprint","IMPRINT",FACE,{"disambiguationData":[TD([[makeQuery(id+"F4.imprint","IMPRINT",EDGE,{"derivedFrom":sQuery(id+"F4.wireOp",EDGE,"E308.12.startCap")}),-1.0]])]});
            var Q13;
            Q13=makeQuery(id+"F4.imprint","IMPRINT",FACE,{"disambiguationData":[TD([[makeQuery(id+"F4.imprint","IMPRINT",EDGE,{"derivedFrom":sQuery(id+"F4.wireOp",EDGE,"E308.13.startCap")}),-1.0]])]});
            var Q14;
            Q14=makeQuery(id+"F4.imprint","IMPRINT",FACE,{"disambiguationData":[TD([[makeQuery(id+"F4.imprint","IMPRINT",EDGE,{"derivedFrom":sQuery(id+"F4.wireOp",EDGE,"E285.0.startCap")}),-1.0]])]});
            var Q15;
            Q15=makeQuery(id+"F4.imprint","IMPRINT",FACE,{"disambiguationData":[TD([[makeQuery(id+"F4.imprint","IMPRINT",EDGE,{"derivedFrom":sQuery(id+"F4.wireOp",EDGE,"E286.MirrorCS")}),-1.0]])]});
            var Q16;
            Q16=makeQuery(id+"F4.imprint","IMPRINT",FACE,{"disambiguationData":[TD([[makeQuery(id+"F4.imprint","IMPRINT",EDGE,{"derivedFrom":sQuery(id+"F4.wireOp",EDGE,"E321.0.startCap")}),-1.0]])]});
            var Q17;
            Q17=makeQuery(id+"F4.imprint","IMPRINT",FACE,{"disambiguationData":[TD([[makeQuery(id+"F4.imprint","IMPRINT",EDGE,{"derivedFrom":sQuery(id+"F4.wireOp",EDGE,"E322.0.startCap")}),-1.0]])]});
            var Q18;
            Q18=makeQuery(id+"F4.imprint","IMPRINT",FACE,{"disambiguationData":[TD([[makeQuery(id+"F4.imprint","IMPRINT",EDGE,{"derivedFrom":sQuery(id+"F4.wireOp",EDGE,"E322.1.startCap")}),-1.0]])]});
            var Q19;
            Q19=makeQuery(id+"F4.imprint","IMPRINT",FACE,{"disambiguationData":[TD([[makeQuery(id+"F4.imprint","IMPRINT",EDGE,{"derivedFrom":sQuery(id+"F4.wireOp",EDGE,"E322.2.startCap")}),-1.0]])]});
            extrude(context, id + "F5", {"entities" : qUnion([Q0, Q1, Q2, Q3, Q4, Q5, Q6, Q7, Q8, Q9, Q10, Q11, Q12, Q13, Q14, Q15, Q16, Q17, Q18, Q19]), "operationType" : NewBodyOperationType.REMOVE, "endBound" : BoundingType.UP_TO_NEXT, "oppositeDirection" : true, "depth" : 25 * mm});
        }
    });
